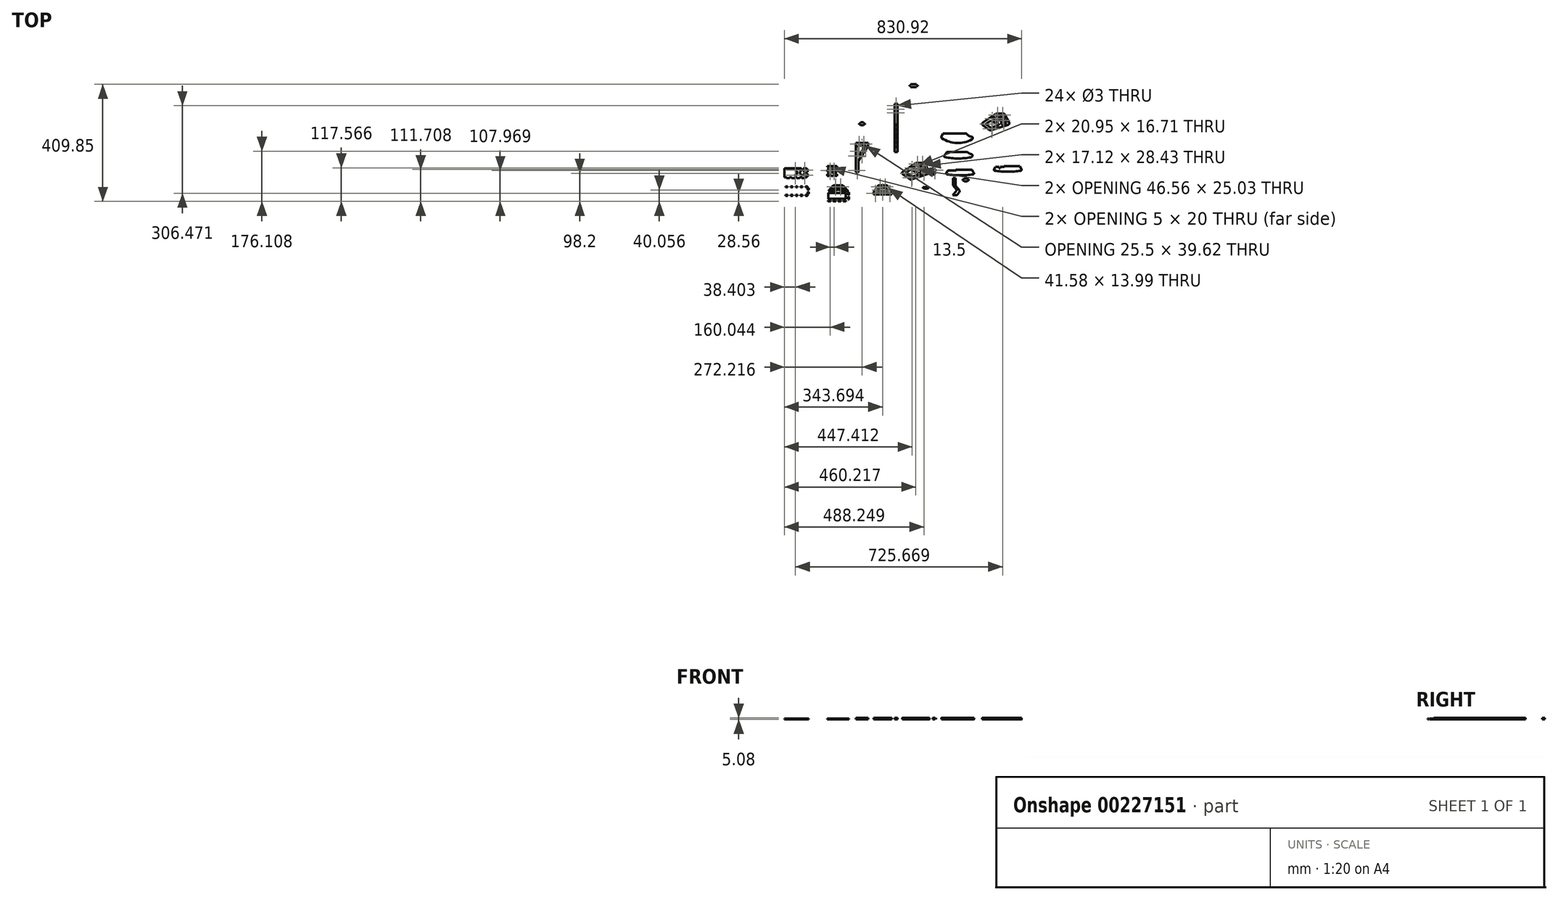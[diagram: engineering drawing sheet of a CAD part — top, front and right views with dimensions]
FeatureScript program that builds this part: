
annotation { "Feature Type Name" : "Feature", "Feature Type Description" : "" }
export const myFeature = defineFeature(function(context is Context, id is Id, definition is map)
    precondition{}
    {
        {
            var Q0;
            Q0=qCreatedBy(makeId("Top.planeOp"),FACE);
            var sketch = newSketch(context, id + "F0", { "sketchPlane" : qUnion([Q0])});
            skCircle(sketch, "E0", {"center": v(-57.8, 43.26) * mm, "radius": 1.5 * mm});
            skLineSegment(sketch, "E1.MirrorCS", {"start": v(-51.3, 50.26) * mm, "end": v(-51.3, 18.26) * mm});
            skLineSegment(sketch, "E2.MirrorCS", {"start": v(-51.3, 47.26) * mm, "end": v(-48.13, 47.26) * mm});
            skLineSegment(sketch, "E3.MirrorCS", {"start": v(-48.13, 47.26) * mm, "end": v(-48.13, 37.26) * mm});
            skLineSegment(sketch, "E4.MirrorCS", {"start": v(-48.13, 37.26) * mm, "end": v(-51.3, 37.26) * mm});
            skLineSegment(sketch, "E5.MirrorCS", {"start": v(-48.13, 31.26) * mm, "end": v(-51.3, 31.26) * mm});
            skLineSegment(sketch, "E6.MirrorCS", {"start": v(-48.13, 21.26) * mm, "end": v(-48.13, 31.26) * mm});
            skLineSegment(sketch, "E7.MirrorCS", {"start": v(-51.3, 21.26) * mm, "end": v(-48.13, 21.26) * mm});
            skCircle(sketch, "E8", {"center": v(-66.8, 34.26) * mm, "radius": 8 * mm});
            skLineSegment(sketch, "E9", {"start": v(-129.3, 50.26) * mm, "end": v(-129.3, 18.26) * mm});
            skLineSegment(sketch, "E10", {"start": v(-121.7, 18.26) * mm, "end": v(-121.7, 15.09) * mm});
            skLineSegment(sketch, "E11", {"start": v(-121.7, 15.09) * mm, "end": v(-111.7, 15.09) * mm});
            skLineSegment(sketch, "E12", {"start": v(-111.7, 15.09) * mm, "end": v(-111.7, 18.26) * mm});
            skLineSegment(sketch, "E13", {"start": v(-104.1, 18.26) * mm, "end": v(-104.1, 15.09) * mm});
            skLineSegment(sketch, "E14", {"start": v(-104.1, 15.09) * mm, "end": v(-94.1, 15.09) * mm});
            skLineSegment(sketch, "E15", {"start": v(-94.1, 15.09) * mm, "end": v(-94.1, 18.26) * mm});
            skLineSegment(sketch, "E16", {"start": v(-86.5, 18.26) * mm, "end": v(-86.5, 15.09) * mm});
            skLineSegment(sketch, "E17", {"start": v(-86.5, 15.09) * mm, "end": v(-76.5, 15.09) * mm});
            skLineSegment(sketch, "E18", {"start": v(-76.5, 15.09) * mm, "end": v(-76.5, 18.26) * mm});
            skLineSegment(sketch, "E19", {"start": v(-68.9, 18.26) * mm, "end": v(-68.9, 15.09) * mm});
            skLineSegment(sketch, "E20", {"start": v(-68.9, 15.09) * mm, "end": v(-58.9, 15.09) * mm});
            skLineSegment(sketch, "E21", {"start": v(-58.9, 15.09) * mm, "end": v(-58.9, 18.26) * mm});
            skCircle(sketch, "E22", {"center": v(-57.8, 43.26) * mm, "radius": 4 * mm, "construction": true});
            skCircle(sketch, "E23", {"center": v(-57.8, 25.36) * mm, "radius": 1.5 * mm});
            skCircle(sketch, "E24", {"center": v(-57.8, 25.36) * mm, "radius": 4 * mm, "construction": true});
            skLineSegment(sketch, "E25", {"start": v(-57.8, 47.26) * mm, "end": v(-57.8, 21.36) * mm, "construction": true});
            skCircle(sketch, "E26", {"center": v(-90.9, 43.26) * mm, "radius": 1.5 * mm});
            skCircle(sketch, "E27", {"center": v(-90.9, 43.26) * mm, "radius": 4 * mm, "construction": true});
            skLineSegment(sketch, "E28", {"start": v(-53.8, 43.26) * mm, "end": v(-94.9, 43.26) * mm, "construction": true});
            skCircle(sketch, "E29", {"center": v(-90.9, 25.36) * mm, "radius": 4 * mm, "construction": true});
            skCircle(sketch, "E30", {"center": v(-90.9, 25.36) * mm, "radius": 1.5 * mm});
            skLineSegment(sketch, "E31", {"start": v(-90.9, 47.26) * mm, "end": v(-90.9, 21.36) * mm, "construction": true});
            skLineSegment(sketch, "E32", {"start": v(-94.9, 25.36) * mm, "end": v(-53.8, 25.36) * mm, "construction": true});
            skCircle(sketch, "E33", {"center": v(-66.8, 34.26) * mm, "radius": 3 * mm});
            skLineSegment(sketch, "E34", {"start": v(-63.8, 34.26) * mm, "end": v(-63.8, 50.26) * mm});
            skLineSegment(sketch, "E35", {"start": v(-69.8, 34.26) * mm, "end": v(-69.8, 50.26) * mm});
            skPoint(sketch, "E36.middle.positionSnap0", {"position": v(-129.3, 34.26) * mm});
            skPoint(sketch, "E36.centerSnap0", {"position": v(-129.3, 34.26) * mm});
            skLineSegment(sketch, "E37", {"start": v(-129.3, 34.26) * mm, "end": v(-51.3, 34.26) * mm, "construction": true});
            skPoint(sketch, "E38.middle", {"position": v(-88.64, 39.7) * mm});
            skLineSegment(sketch, "E39.bottom", {"start": v(-84.41, 39.34) * mm, "end": v(-87.41, 39.34) * mm});
            skLineSegment(sketch, "E39.top", {"start": v(-84.41, 29.18) * mm, "end": v(-87.41, 29.18) * mm});
            skLineSegment(sketch, "E39.left", {"start": v(-84.41, 39.34) * mm, "end": v(-84.41, 29.18) * mm});
            skLineSegment(sketch, "E39.right", {"start": v(-87.41, 39.34) * mm, "end": v(-87.41, 29.18) * mm});
            skPoint(sketch, "E39.middle", {"position": v(-85.91, 34.26) * mm});
            skLineSegment(sketch, "E40.bottom", {"start": v(-47.84, -16.11) * mm, "end": v(-125.84, -16.11) * mm});
            skLineSegment(sketch, "E40.top", {"start": v(-47.84, -43.11) * mm, "end": v(-125.84, -43.11) * mm});
            skLineSegment(sketch, "E40.left", {"start": v(-47.84, -16.11) * mm, "end": v(-47.84, -43.11) * mm});
            skLineSegment(sketch, "E41.bottom", {"start": v(-47.84, -19.11) * mm, "end": v(-44.66, -19.11) * mm});
            skLineSegment(sketch, "E41.top", {"start": v(-47.84, -26.61) * mm, "end": v(-44.66, -26.61) * mm});
            skLineSegment(sketch, "E41.left", {"start": v(-47.84, -19.11) * mm, "end": v(-47.84, -26.61) * mm});
            skLineSegment(sketch, "E41.right", {"start": v(-44.66, -19.11) * mm, "end": v(-44.66, -26.61) * mm});
            skLineSegment(sketch, "E42", {"start": v(-125.84, -43.11) * mm, "end": v(-125.84, -46.29) * mm});
            skLineSegment(sketch, "E43", {"start": v(-125.84, -46.29) * mm, "end": v(-118.24, -46.29) * mm});
            skLineSegment(sketch, "E44", {"start": v(-118.24, -46.29) * mm, "end": v(-118.24, -43.11) * mm});
            skLineSegment(sketch, "E45", {"start": v(-108.24, -43.11) * mm, "end": v(-108.24, -46.27) * mm});
            skLineSegment(sketch, "E46", {"start": v(-108.24, -46.27) * mm, "end": v(-100.64, -46.27) * mm});
            skLineSegment(sketch, "E47", {"start": v(-100.64, -46.27) * mm, "end": v(-100.64, -43.1) * mm});
            skLineSegment(sketch, "E48", {"start": v(-90.64, -43.11) * mm, "end": v(-90.64, -46.27) * mm});
            skLineSegment(sketch, "E49", {"start": v(-90.64, -46.27) * mm, "end": v(-83.04, -46.27) * mm});
            skLineSegment(sketch, "E50", {"start": v(-83.04, -46.27) * mm, "end": v(-83.04, -43.11) * mm});
            skLineSegment(sketch, "E51", {"start": v(-73.04, -43.11) * mm, "end": v(-73.04, -46.29) * mm});
            skLineSegment(sketch, "E52", {"start": v(-73.04, -46.29) * mm, "end": v(-65.44, -46.29) * mm});
            skLineSegment(sketch, "E53", {"start": v(-65.44, -46.29) * mm, "end": v(-65.44, -43.11) * mm});
            skLineSegment(sketch, "E54", {"start": v(-55.44, -43.11) * mm, "end": v(-55.44, -46.29) * mm});
            skLineSegment(sketch, "E55", {"start": v(-55.44, -46.29) * mm, "end": v(-47.84, -46.29) * mm});
            skLineSegment(sketch, "E56", {"start": v(-47.84, -46.29) * mm, "end": v(-47.84, -43.11) * mm});
            skLineSegment(sketch, "E57", {"start": v(-125.84, -43.11) * mm, "end": v(-125.84, -16.11) * mm});
            skLineSegment(sketch, "E58.MirrorCS", {"start": v(-125.84, -12.94) * mm, "end": v(-118.24, -12.94) * mm});
            skLineSegment(sketch, "E59.MirrorCS", {"start": v(-125.84, -16.11) * mm, "end": v(-125.84, -12.94) * mm});
            skLineSegment(sketch, "E60.MirrorCS", {"start": v(-118.24, -12.94) * mm, "end": v(-118.24, -16.11) * mm});
            skLineSegment(sketch, "E61.MirrorCS", {"start": v(-108.24, -12.96) * mm, "end": v(-100.64, -12.96) * mm});
            skLineSegment(sketch, "E62.MirrorCS", {"start": v(-108.24, -16.11) * mm, "end": v(-108.24, -12.96) * mm});
            skLineSegment(sketch, "E63.MirrorCS", {"start": v(-100.64, -12.96) * mm, "end": v(-100.64, -16.13) * mm});
            skLineSegment(sketch, "E64.MirrorCS", {"start": v(-90.64, -12.96) * mm, "end": v(-83.04, -12.96) * mm});
            skLineSegment(sketch, "E65.MirrorCS", {"start": v(-90.64, -16.11) * mm, "end": v(-90.64, -12.96) * mm});
            skLineSegment(sketch, "E66.MirrorCS", {"start": v(-83.04, -12.96) * mm, "end": v(-83.04, -16.11) * mm});
            skLineSegment(sketch, "E67.MirrorCS", {"start": v(-73.04, -12.94) * mm, "end": v(-65.44, -12.94) * mm});
            skLineSegment(sketch, "E68.MirrorCS", {"start": v(-73.04, -16.11) * mm, "end": v(-73.04, -12.94) * mm});
            skLineSegment(sketch, "E69.MirrorCS", {"start": v(-65.44, -12.94) * mm, "end": v(-65.44, -16.11) * mm});
            skLineSegment(sketch, "E70.MirrorCS", {"start": v(-55.44, -16.11) * mm, "end": v(-55.44, -12.94) * mm});
            skLineSegment(sketch, "E71.MirrorCS", {"start": v(-55.44, -12.94) * mm, "end": v(-47.84, -12.94) * mm});
            skLineSegment(sketch, "E72.MirrorCS", {"start": v(-47.84, -12.94) * mm, "end": v(-47.84, -16.11) * mm});
            skLineSegment(sketch, "E73.MirrorCS", {"start": v(-47.84, -32.61) * mm, "end": v(-44.66, -32.61) * mm});
            skLineSegment(sketch, "E74.MirrorCS", {"start": v(-44.66, -40.11) * mm, "end": v(-44.66, -32.61) * mm});
            skLineSegment(sketch, "E75.MirrorCS", {"start": v(-47.84, -40.11) * mm, "end": v(-44.66, -40.11) * mm});
            skLineSegment(sketch, "E76.MirrorCS", {"start": v(93.67, -30.61) * mm, "end": v(93.67, -62.61) * mm});
            skLineSegment(sketch, "E77.MirrorCS", {"start": v(97.56, -25.43) * mm, "end": v(98.56, -25.43) * mm});
            skLineSegment(sketch, "E78.MirrorCS", {"start": v(96.85, -33.61) * mm, "end": v(96.85, -43.61) * mm});
            skLineSegment(sketch, "E79.MirrorCS", {"start": v(96.85, -59.61) * mm, "end": v(96.85, -49.61) * mm});
            skLineSegment(sketch, "E80", {"start": v(15.67, -30.61) * mm, "end": v(15.67, -62.61) * mm});
            skLineSegment(sketch, "E81", {"start": v(23.27, -62.61) * mm, "end": v(23.27, -65.79) * mm});
            skLineSegment(sketch, "E82", {"start": v(23.27, -65.79) * mm, "end": v(33.27, -65.79) * mm});
            skLineSegment(sketch, "E83", {"start": v(33.27, -65.79) * mm, "end": v(33.27, -62.61) * mm});
            skLineSegment(sketch, "E84", {"start": v(40.87, -62.61) * mm, "end": v(40.87, -65.79) * mm});
            skLineSegment(sketch, "E85", {"start": v(40.87, -65.79) * mm, "end": v(50.87, -65.79) * mm});
            skLineSegment(sketch, "E86", {"start": v(50.87, -65.79) * mm, "end": v(50.87, -62.61) * mm});
            skLineSegment(sketch, "E87", {"start": v(58.47, -62.61) * mm, "end": v(58.47, -65.79) * mm});
            skLineSegment(sketch, "E88", {"start": v(58.47, -65.79) * mm, "end": v(68.47, -65.79) * mm});
            skLineSegment(sketch, "E89", {"start": v(68.47, -65.79) * mm, "end": v(68.47, -62.61) * mm});
            skLineSegment(sketch, "E90", {"start": v(76.07, -62.61) * mm, "end": v(76.07, -65.79) * mm});
            skLineSegment(sketch, "E91", {"start": v(76.07, -65.79) * mm, "end": v(86.07, -65.79) * mm});
            skLineSegment(sketch, "E92", {"start": v(86.07, -65.79) * mm, "end": v(86.07, -62.61) * mm});
            skLineSegment(sketch, "E93", {"start": v(15.67, -30.61) * mm, "end": v(93.67, -30.61) * mm});
            skLineSegment(sketch, "E94", {"start": v(15.67, -62.61) * mm, "end": v(93.67, -62.61) * mm});
            skLineSegment(sketch, "E95", {"start": v(96.85, -33.61) * mm, "end": v(93.67, -33.61) * mm});
            skLineSegment(sketch, "E96", {"start": v(96.85, -43.61) * mm, "end": v(93.67, -43.61) * mm});
            skLineSegment(sketch, "E97", {"start": v(96.85, -49.61) * mm, "end": v(93.67, -49.61) * mm});
            skLineSegment(sketch, "E98", {"start": v(96.85, -59.61) * mm, "end": v(93.67, -59.61) * mm});
            skLineSegment(sketch, "E99.left", {"start": v(15.67, -62.61) * mm, "end": v(15.67, -30.61) * mm});
            skLineSegment(sketch, "E100.bottom", {"start": v(75.3, -9.86) * mm, "end": v(42.75, -9.86) * mm});
            skLineSegment(sketch, "E100.left", {"start": v(75.3, -9.86) * mm, "end": v(75.3, -18.86) * mm});
            skLineSegment(sketch, "E100.right", {"start": v(42.75, -9.86) * mm, "end": v(42.75, -18.86) * mm});
            skPoint(sketch, "E100.middle", {"position": v(59.03, -14.36) * mm});
            skCircle(sketch, "E101", {"center": v(67.78, -14.36) * mm, "radius": 1.5 * mm});
            skCircle(sketch, "E102.MirrorC", {"center": v(50.28, -14.36) * mm, "radius": 1.5 * mm});
            skLineSegment(sketch, "E103", {"start": v(42.75, -18.86) * mm, "end": v(42.75, -30.61) * mm});
            skLineSegment(sketch, "E104", {"start": v(75.3, -18.86) * mm, "end": v(75.3, -30.61) * mm});
            skPoint(sketch, "E105.middle", {"position": v(54.67, -46.61) * mm});
            skPoint(sketch, "E105.middle.positionSnap0", {"position": v(54.67, -30.61) * mm});
            skPoint(sketch, "E105.middle.positionSnap1", {"position": v(15.67, -46.61) * mm});
            skPoint(sketch, "E105.centerSnap0", {"position": v(54.67, -30.61) * mm});
            skPoint(sketch, "E105.centerSnap1", {"position": v(15.67, -46.61) * mm});
            skLineSegment(sketch, "E106", {"start": v(75.3, -9.86) * mm, "end": v(93.67, -30.61) * mm});
            skLineSegment(sketch, "E107.bottom", {"start": v(50.98, 58.18) * mm, "end": v(23.98, 58.18) * mm});
            skLineSegment(sketch, "E107.top", {"start": v(50.98, 26.18) * mm, "end": v(23.98, 26.18) * mm});
            skLineSegment(sketch, "E107.left", {"start": v(50.98, 58.18) * mm, "end": v(50.98, 26.18) * mm});
            skLineSegment(sketch, "E107.right", {"start": v(23.98, 58.18) * mm, "end": v(23.98, 26.18) * mm});
            skPoint(sketch, "E107.middle", {"position": v(37.48, 42.18) * mm});
            skLineSegment(sketch, "E108", {"start": v(37.48, 58.18) * mm, "end": v(37.48, 26.18) * mm, "construction": true});
            skLineSegment(sketch, "E109", {"start": v(34.48, 26.18) * mm, "end": v(34.48, 23) * mm});
            skLineSegment(sketch, "E110", {"start": v(34.48, 23) * mm, "end": v(40.48, 23) * mm});
            skLineSegment(sketch, "E111", {"start": v(40.48, 23) * mm, "end": v(40.48, 26.18) * mm});
            skLineSegment(sketch, "E112", {"start": v(47.98, 23) * mm, "end": v(47.98, 26.18) * mm});
            skLineSegment(sketch, "E113", {"start": v(50.98, 45.18) * mm, "end": v(54.3, 45.18) * mm});
            skLineSegment(sketch, "E114", {"start": v(54.3, 45.18) * mm, "end": v(54.3, 39.18) * mm});
            skLineSegment(sketch, "E115", {"start": v(54.3, 39.18) * mm, "end": v(50.98, 39.18) * mm});
            skLineSegment(sketch, "E116", {"start": v(50.98, 58.18) * mm, "end": v(54.3, 58.18) * mm});
            skLineSegment(sketch, "E117", {"start": v(54.3, 58.18) * mm, "end": v(54.3, 55.18) * mm});
            skLineSegment(sketch, "E118", {"start": v(54.3, 55.18) * mm, "end": v(50.98, 55.18) * mm});
            skLineSegment(sketch, "E119", {"start": v(23.98, 42.18) * mm, "end": v(50.98, 42.18) * mm, "construction": true});
            skLineSegment(sketch, "E120.MirrorCS", {"start": v(54.3, 29.18) * mm, "end": v(50.98, 29.18) * mm});
            skLineSegment(sketch, "E121.MirrorCS", {"start": v(54.3, 26.18) * mm, "end": v(54.3, 29.18) * mm});
            skLineSegment(sketch, "E122.MirrorCS", {"start": v(50.98, 26.18) * mm, "end": v(54.3, 26.18) * mm});
            skLineSegment(sketch, "E123.MirrorCS", {"start": v(23.98, 58.18) * mm, "end": v(20.67, 58.18) * mm});
            skLineSegment(sketch, "E124.MirrorCS", {"start": v(20.67, 55.18) * mm, "end": v(23.98, 55.18) * mm});
            skLineSegment(sketch, "E125.MirrorCS", {"start": v(20.67, 58.18) * mm, "end": v(20.67, 55.18) * mm});
            skLineSegment(sketch, "E126.MirrorCS", {"start": v(23.98, 45.18) * mm, "end": v(20.67, 45.18) * mm});
            skLineSegment(sketch, "E127.MirrorCS", {"start": v(20.67, 45.18) * mm, "end": v(20.67, 39.18) * mm});
            skLineSegment(sketch, "E128.MirrorCS", {"start": v(20.67, 39.18) * mm, "end": v(23.98, 39.18) * mm});
            skLineSegment(sketch, "E129.MirrorCS", {"start": v(20.67, 29.18) * mm, "end": v(23.98, 29.18) * mm});
            skLineSegment(sketch, "E130.MirrorCS", {"start": v(23.98, 26.18) * mm, "end": v(20.67, 26.18) * mm});
            skLineSegment(sketch, "E131.MirrorCS", {"start": v(20.67, 26.18) * mm, "end": v(20.67, 29.18) * mm});
            skLineSegment(sketch, "E132", {"start": v(47.98, 23) * mm, "end": v(54.3, 23) * mm});
            skLineSegment(sketch, "E133", {"start": v(54.3, 23) * mm, "end": v(54.3, 26.18) * mm});
            skLineSegment(sketch, "E134.MirrorCS", {"start": v(26.98, 23) * mm, "end": v(26.98, 26.18) * mm});
            skLineSegment(sketch, "E135.MirrorCS", {"start": v(26.98, 23) * mm, "end": v(20.67, 23) * mm});
            skLineSegment(sketch, "E136.MirrorCS", {"start": v(20.67, 23) * mm, "end": v(20.67, 26.18) * mm});
            skLineSegment(sketch, "E137", {"start": v(-86.84, -16.11) * mm, "end": v(-86.84, -43.11) * mm, "construction": true});
            skLineSegment(sketch, "E138", {"start": v(-125.84, -29.61) * mm, "end": v(-47.84, -29.61) * mm, "construction": true});
            skLineSegment(sketch, "E139", {"start": v(-129.3, 50.26) * mm, "end": v(-51.3, 50.26) * mm});
            skLineSegment(sketch, "E140", {"start": v(-129.3, 18.26) * mm, "end": v(-51.3, 18.26) * mm});
            skCircle(sketch, "E141", {"center": v(125.66, 93.63) * mm, "radius": 1.5 * mm});
            skCircle(sketch, "E142", {"center": v(125.66, 42.93) * mm, "radius": 1.5 * mm});
            skLineSegment(sketch, "E143", {"start": v(125.66, 93.63) * mm, "end": v(125.66, 42.93) * mm});
            skPoint(sketch, "E144.middle", {"position": v(125.66, 68.28) * mm});
            skLineSegment(sketch, "E145.top", {"start": v(121.16, 139.13) * mm, "end": v(155.66, 139.13) * mm});
            skLineSegment(sketch, "E145.left", {"start": v(121.16, 130.13) * mm, "end": v(121.16, 139.13) * mm});
            skLineSegment(sketch, "E145.right", {"start": v(155.66, 130.13) * mm, "end": v(155.66, 139.13) * mm});
            skCircle(sketch, "E146", {"center": v(131.66, 134.63) * mm, "radius": 1.5 * mm});
            skPoint(sketch, "E146.centerSnap0", {"position": v(121.16, 134.63) * mm});
            skLineSegment(sketch, "E147", {"start": v(131.66, 134.63) * mm, "end": v(149.16, 134.63) * mm});
            skCircle(sketch, "E148", {"center": v(149.16, 134.63) * mm, "radius": 1.5 * mm});
            skLineSegment(sketch, "E149", {"start": v(121.16, 130.13) * mm, "end": v(155.66, 130.13) * mm});
            skLineSegment(sketch, "E150", {"start": v(121.16, 130.13) * mm, "end": v(121.16, 36.43) * mm});
            skLineSegment(sketch, "E151", {"start": v(121.16, 36.43) * mm, "end": v(130.16, 36.43) * mm});
            skLineSegment(sketch, "E152", {"start": v(130.16, 36.43) * mm, "end": v(130.16, 130.13) * mm});
            skLineSegment(sketch, "E153", {"start": v(164.66, 130.13) * mm, "end": v(130.16, 76.52) * mm});
            skLineSegment(sketch, "E154", {"start": v(155.66, 130.13) * mm, "end": v(130.16, 90.5) * mm});
            skLineSegment(sketch, "E155", {"start": v(164.66, 130.13) * mm, "end": v(164.66, 139.13) * mm});
            skLineSegment(sketch, "E156", {"start": v(164.66, 139.13) * mm, "end": v(155.66, 139.13) * mm});
            skLineSegment(sketch, "E157.bottom", {"start": v(182.48, -32.73) * mm, "end": v(246.28, -32.73) * mm});
            skLineSegment(sketch, "E157.top", {"start": v(182.48, -41.73) * mm, "end": v(246.28, -41.73) * mm});
            skLineSegment(sketch, "E157.left", {"start": v(182.48, -32.73) * mm, "end": v(182.48, -41.73) * mm});
            skLineSegment(sketch, "E157.right", {"start": v(246.28, -32.73) * mm, "end": v(246.28, -41.73) * mm});
            skCircle(sketch, "E158", {"center": v(188.98, -37.23) * mm, "radius": 1.5 * mm});
            skPoint(sketch, "E158.centerSnap0", {"position": v(182.48, -37.23) * mm});
            skCircle(sketch, "E159", {"center": v(239.78, -37.23) * mm, "radius": 1.5 * mm});
            skLineSegment(sketch, "E160.bottom", {"start": v(199.13, -9.74) * mm, "end": v(229.63, -9.74) * mm});
            skLineSegment(sketch, "E160.top", {"start": v(199.13, -18.74) * mm, "end": v(229.63, -18.74) * mm});
            skLineSegment(sketch, "E160.left", {"start": v(199.13, -9.74) * mm, "end": v(199.13, -18.74) * mm});
            skLineSegment(sketch, "E160.right", {"start": v(229.63, -9.74) * mm, "end": v(229.63, -18.74) * mm});
            skLineSegment(sketch, "E161", {"start": v(199.13, -9.74) * mm, "end": v(182.48, -32.73) * mm});
            skLineSegment(sketch, "E162", {"start": v(199.13, -18.74) * mm, "end": v(189, -32.73) * mm, "construction": true});
            skLineSegment(sketch, "E163", {"start": v(229.63, -9.74) * mm, "end": v(246.28, -32.73) * mm});
            skLineSegment(sketch, "E164", {"start": v(229.63, -18.74) * mm, "end": v(239.77, -32.73) * mm, "construction": true});
            skCircle(sketch, "E165", {"center": v(205.63, -14.24) * mm, "radius": 1.5 * mm});
            skPoint(sketch, "E165.centerSnap0", {"position": v(199.13, -14.24) * mm});
            skCircle(sketch, "E166", {"center": v(223.13, -14.24) * mm, "radius": 1.5 * mm});
            skPoint(sketch, "E166.centerSnap0", {"position": v(229.63, -14.24) * mm});
            skLineSegment(sketch, "E167", {"start": v(214.38, -18.74) * mm, "end": v(214.38, -32.73) * mm, "construction": true});
            skLineSegment(sketch, "E168", {"start": v(193.6, -32.73) * mm, "end": v(203.73, -18.74) * mm});
            skLineSegment(sketch, "E169.MirrorCS", {"start": v(235.17, -32.73) * mm, "end": v(225.04, -18.74) * mm});
            skLineSegment(sketch, "E170.bottom", {"start": v(330.61, 69.13) * mm, "end": v(361.11, 69.13) * mm});
            skLineSegment(sketch, "E170.top", {"start": v(330.61, 60.13) * mm, "end": v(361.11, 60.13) * mm});
            skLineSegment(sketch, "E170.left", {"start": v(330.61, 69.13) * mm, "end": v(330.61, 60.13) * mm});
            skLineSegment(sketch, "E170.right", {"start": v(361.11, 69.13) * mm, "end": v(361.11, 60.13) * mm});
            skCircle(sketch, "E171", {"center": v(337.11, 64.63) * mm, "radius": 1.5 * mm});
            skPoint(sketch, "E171.centerSnap0", {"position": v(330.61, 64.63) * mm});
            skCircle(sketch, "E172", {"center": v(354.61, 64.63) * mm, "radius": 1.5 * mm});
            skPoint(sketch, "E172.centerSnap0", {"position": v(361.11, 64.63) * mm});
            skLineSegment(sketch, "E173", {"start": v(354.61, 64.63) * mm, "end": v(364.99, 32.38) * mm, "construction": true});
            skCircle(sketch, "E174", {"center": v(364.99, 32.38) * mm, "radius": 2.25 * mm});
            skLineSegment(sketch, "E175", {"start": v(364.99, 32.38) * mm, "end": v(316.44, 16.76) * mm, "construction": true});
            skCircle(sketch, "E176", {"center": v(316.44, 16.76) * mm, "radius": 1.5 * mm});
            skLineSegment(sketch, "E177", {"start": v(309.08, 18.42) * mm, "end": v(311.72, 10.2) * mm});
            skLineSegment(sketch, "E178", {"start": v(311.72, 10.2) * mm, "end": v(373.36, 30.03) * mm});
            skLineSegment(sketch, "E179", {"start": v(373.36, 30.03) * mm, "end": v(370.72, 38.25) * mm});
            skLineSegment(sketch, "E180", {"start": v(370.72, 38.25) * mm, "end": v(309.08, 18.42) * mm});
            skLineSegment(sketch, "E181", {"start": v(361.11, 69.13) * mm, "end": v(380.2, 32.23) * mm});
            skLineSegment(sketch, "E182", {"start": v(380.2, 32.23) * mm, "end": v(373.36, 30.03) * mm});
            skLineSegment(sketch, "E183", {"start": v(367.5, 37.21) * mm, "end": v(355.64, 60.13) * mm});
            skLineSegment(sketch, "E184", {"start": v(309.08, 18.42) * mm, "end": v(304.62, 7.92) * mm});
            skLineSegment(sketch, "E185", {"start": v(304.62, 7.92) * mm, "end": v(311.72, 10.2) * mm});
            skCircle(sketch, "E186", {"center": v(397.86, 43.41) * mm, "radius": 1.5 * mm});
            skCircle(sketch, "E187", {"center": v(397.86, 43.41) * mm, "radius": 3 * mm});
            skCircle(sketch, "E188", {"center": v(394.3, 31.54) * mm, "radius": 2.25 * mm});
            skCircle(sketch, "E189", {"center": v(394.3, 31.54) * mm, "radius": 3.75 * mm});
            skLineSegment(sketch, "E190.bottom", {"start": v(257.06, 256.54) * mm, "end": v(267.22, 256.54) * mm});
            skLineSegment(sketch, "E190.top", {"start": v(257.06, 106.54) * mm, "end": v(267.22, 106.54) * mm});
            skLineSegment(sketch, "E190.left", {"start": v(257.06, 256.54) * mm, "end": v(257.06, 106.54) * mm});
            skLineSegment(sketch, "E190.right", {"start": v(267.22, 256.54) * mm, "end": v(267.22, 106.54) * mm});
            skCircle(sketch, "E191", {"center": v(262.14, 256.54) * mm, "radius": 1.5 * mm});
            skCircle(sketch, "E192", {"center": v(262.14, 243.84) * mm, "radius": 1.5 * mm});
            skLineSegment(sketch, "E193", {"start": v(257.06, 256.54) * mm, "end": v(257.06, 276.54) * mm});
            skLineSegment(sketch, "E194", {"start": v(257.06, 276.54) * mm, "end": v(267.22, 276.54) * mm});
            skLineSegment(sketch, "E195", {"start": v(267.22, 276.54) * mm, "end": v(267.22, 256.54) * mm});
            skCircle(sketch, "E196.MirrorC", {"center": v(262.14, 269.24) * mm, "radius": 1.5 * mm});
            skPoint(sketch, "E197.centerSnap0", {"position": v(262.14, 106.54) * mm});
            skLineSegment(sketch, "E198.bottom", {"start": v(264.14, 203.84) * mm, "end": v(260.14, 203.84) * mm});
            skLineSegment(sketch, "E198.top", {"start": v(264.14, 198.76) * mm, "end": v(260.14, 198.76) * mm});
            skLineSegment(sketch, "E198.left", {"start": v(264.14, 203.84) * mm, "end": v(264.14, 198.76) * mm});
            skLineSegment(sketch, "E198.right", {"start": v(260.14, 203.84) * mm, "end": v(260.14, 198.76) * mm});
            skPoint(sketch, "E198.middle", {"position": v(262.14, 201.3) * mm});
            skLineSegment(sketch, "E199.bottom", {"start": v(264.14, 188.76) * mm, "end": v(260.14, 188.76) * mm});
            skLineSegment(sketch, "E199.top", {"start": v(264.14, 183.68) * mm, "end": v(260.14, 183.68) * mm});
            skLineSegment(sketch, "E199.left", {"start": v(264.14, 188.76) * mm, "end": v(264.14, 183.68) * mm});
            skLineSegment(sketch, "E199.right", {"start": v(260.14, 188.76) * mm, "end": v(260.14, 183.68) * mm});
            skPoint(sketch, "E199.middle", {"position": v(262.14, 186.22) * mm});
            skPoint(sketch, "E199.middle.positionSnap0", {"position": v(262.14, 198.76) * mm});
            skPoint(sketch, "E199.centerSnap0", {"position": v(262.14, 198.76) * mm});
            skLineSegment(sketch, "E200.bottom", {"start": v(264.14, 173.68) * mm, "end": v(260.14, 173.68) * mm});
            skLineSegment(sketch, "E200.top", {"start": v(264.14, 168.6) * mm, "end": v(260.14, 168.6) * mm});
            skLineSegment(sketch, "E200.left", {"start": v(264.14, 173.68) * mm, "end": v(264.14, 168.6) * mm});
            skLineSegment(sketch, "E200.right", {"start": v(260.14, 173.68) * mm, "end": v(260.14, 168.6) * mm});
            skPoint(sketch, "E200.middle", {"position": v(262.14, 171.14) * mm});
            skPoint(sketch, "E200.middle.positionSnap0", {"position": v(262.14, 183.68) * mm});
            skPoint(sketch, "E200.centerSnap0", {"position": v(262.14, 183.68) * mm});
            skLineSegment(sketch, "E201.bottom", {"start": v(264.14, 158.6) * mm, "end": v(260.14, 158.6) * mm});
            skLineSegment(sketch, "E201.top", {"start": v(264.14, 153.52) * mm, "end": v(260.14, 153.52) * mm});
            skLineSegment(sketch, "E201.left", {"start": v(264.14, 158.6) * mm, "end": v(264.14, 153.52) * mm});
            skLineSegment(sketch, "E201.right", {"start": v(260.14, 158.6) * mm, "end": v(260.14, 153.52) * mm});
            skPoint(sketch, "E201.middle", {"position": v(262.14, 156.06) * mm});
            skPoint(sketch, "E201.middle.positionSnap0", {"position": v(262.14, 168.6) * mm});
            skPoint(sketch, "E201.centerSnap0", {"position": v(262.14, 168.6) * mm});
            skPoint(sketch, "E202.middle.positionSnap0", {"position": v(262.14, 153.52) * mm});
            skPoint(sketch, "E202.centerSnap0", {"position": v(262.14, 153.52) * mm});
            skLineSegment(sketch, "E203.bottom", {"start": v(137.72, 210.77) * mm, "end": v(147.24, 210.77) * mm});
            skLineSegment(sketch, "E203.top", {"start": v(137.72, 200.6) * mm, "end": v(147.24, 200.6) * mm});
            skLineSegment(sketch, "E203.left", {"start": v(137.72, 210.77) * mm, "end": v(137.72, 200.6) * mm});
            skLineSegment(sketch, "E203.right", {"start": v(147.24, 210.77) * mm, "end": v(147.24, 200.6) * mm});
            skLineSegment(sketch, "E204.bottom", {"start": v(147.24, 207.69) * mm, "end": v(152.32, 207.69) * mm});
            skLineSegment(sketch, "E204.top", {"start": v(147.24, 203.69) * mm, "end": v(152.32, 203.69) * mm});
            skLineSegment(sketch, "E204.left", {"start": v(147.24, 207.69) * mm, "end": v(147.24, 203.69) * mm});
            skLineSegment(sketch, "E204.right", {"start": v(152.32, 207.69) * mm, "end": v(152.32, 203.69) * mm});
            skLineSegment(sketch, "E205", {"start": v(142.48, 210.77) * mm, "end": v(142.48, 200.6) * mm, "construction": true});
            skLineSegment(sketch, "E206.MirrorCS", {"start": v(137.72, 207.69) * mm, "end": v(132.64, 207.69) * mm});
            skLineSegment(sketch, "E207.MirrorCS", {"start": v(132.64, 207.69) * mm, "end": v(132.64, 203.69) * mm});
            skLineSegment(sketch, "E208.MirrorCS", {"start": v(137.72, 203.69) * mm, "end": v(132.64, 203.69) * mm});
            skLineSegment(sketch, "E209", {"start": v(426.01, 171.7) * mm, "end": v(508.81, 171.7) * mm});
            skLineSegment(sketch, "E210", {"start": v(426.01, 171.7) * mm, "end": v(419.29, 157.26) * mm});
            skArc(sketch, "E211", {"start": v(508.81, 171.7) * mm, "mid": v(517.5, 163.5) * mm, "end": v(529.1, 160.7) * mm});
            skArc(sketch, "E212", {"start": v(529.09, 151.73) * mm, "mid": v(529.79, 156.21) * mm, "end": v(529.1, 160.7) * mm});
            skArc(sketch, "E213", {"start": v(419.29, 157.26) * mm, "mid": v(473.39, 138.7) * mm, "end": v(529.09, 151.73) * mm});
            skArc(sketch, "E214", {"start": v(427.52, 90.3) * mm, "mid": v(475.83, 84.48) * mm, "end": v(524.31, 88.6) * mm});
            skArc(sketch, "E215", {"start": v(524.31, 88.6) * mm, "mid": v(528.75, 92.71) * mm, "end": v(528.27, 98.75) * mm});
            skArc(sketch, "E216", {"start": v(510.32, 107.55) * mm, "mid": v(518.66, 101.85) * mm, "end": v(528.27, 98.75) * mm});
            skLineSegment(sketch, "E217", {"start": v(427.52, 90.3) * mm, "end": v(439.57, 107.55) * mm});
            skLineSegment(sketch, "E218", {"start": v(439.57, 107.55) * mm, "end": v(510.32, 107.55) * mm});
            skLineSegment(sketch, "E219", {"start": v(472.05, 45.33) * mm, "end": v(527.34, 45.33) * mm});
            skLineSegment(sketch, "E220", {"start": v(527.34, 45.33) * mm, "end": v(536.47, 29.52) * mm});
            skLineSegment(sketch, "E221", {"start": v(472.05, 45.33) * mm, "end": v(471.13, 41.92) * mm});
            skLineSegment(sketch, "E222", {"start": v(471.13, 41.92) * mm, "end": v(442.34, 41.92) * mm});
            skLineSegment(sketch, "E223", {"start": v(442.34, 41.92) * mm, "end": v(435.18, 29.52) * mm});
            skArc(sketch, "E224", {"start": v(435.18, 29.52) * mm, "mid": v(485.83, 25.33) * mm, "end": v(536.47, 29.52) * mm});
            skLineSegment(sketch, "E225", {"start": v(460.14, -44.05) * mm, "end": v(475.14, -44.05) * mm});
            skLineSegment(sketch, "E226", {"start": v(475.14, -44.05) * mm, "end": v(485.93, -31.18) * mm});
            skLineSegment(sketch, "E227", {"start": v(485.93, -31.18) * mm, "end": v(469.2, -9.36) * mm});
            skLineSegment(sketch, "E228", {"start": v(460.14, -44.05) * mm, "end": v(474.82, -26.55) * mm});
            skLineSegment(sketch, "E229", {"start": v(474.82, -26.55) * mm, "end": v(461.63, -9.36) * mm});
            skLineSegment(sketch, "E230", {"start": v(461.63, -9.36) * mm, "end": v(469.2, -9.36) * mm});
            skLineSegment(sketch, "E231", {"start": v(640.47, 58.15) * mm, "end": v(694.56, 58.15) * mm});
            skLineSegment(sketch, "E232", {"start": v(694.56, 58.15) * mm, "end": v(703.69, 42.34) * mm});
            skLineSegment(sketch, "E233", {"start": v(640.47, 58.15) * mm, "end": v(639.56, 54.74) * mm});
            skLineSegment(sketch, "E234", {"start": v(639.56, 54.74) * mm, "end": v(609.56, 54.74) * mm});
            skLineSegment(sketch, "E235", {"start": v(609.56, 54.74) * mm, "end": v(602.4, 42.34) * mm});
            skArc(sketch, "E236", {"start": v(602.4, 42.34) * mm, "mid": v(653.04, 38.15) * mm, "end": v(703.69, 42.34) * mm});
            skLineSegment(sketch, "E237.bottom", {"start": v(623.06, 54.74) * mm, "end": v(626.06, 54.74) * mm});
            skLineSegment(sketch, "E237.top", {"start": v(623.06, 49.74) * mm, "end": v(626.06, 49.74) * mm});
            skLineSegment(sketch, "E237.left", {"start": v(623.06, 54.74) * mm, "end": v(623.06, 49.74) * mm});
            skLineSegment(sketch, "E237.right", {"start": v(626.06, 54.74) * mm, "end": v(626.06, 49.74) * mm});
            skLineSegment(sketch, "E238.bottom", {"start": v(466.14, -44.05) * mm, "end": v(469.14, -44.05) * mm});
            skLineSegment(sketch, "E238.top", {"start": v(466.14, -49.05) * mm, "end": v(469.14, -49.05) * mm});
            skLineSegment(sketch, "E238.left", {"start": v(466.14, -44.05) * mm, "end": v(466.14, -49.05) * mm});
            skLineSegment(sketch, "E238.right", {"start": v(469.14, -44.05) * mm, "end": v(469.14, -49.05) * mm});
            skLineSegment(sketch, "E239", {"start": v(461.63, -9.36) * mm, "end": v(460.65, -9.36) * mm});
            skLineSegment(sketch, "E240", {"start": v(460.65, -9.36) * mm, "end": v(460.65, 15.64) * mm});
            skLineSegment(sketch, "E241", {"start": v(465.41, -9.36) * mm, "end": v(465.41, 15.64) * mm, "construction": true});
            skLineSegment(sketch, "E242", {"start": v(465.41, 15.64) * mm, "end": v(460.65, 15.64) * mm});
            skLineSegment(sketch, "E243.MirrorCS", {"start": v(469.2, -9.36) * mm, "end": v(470.17, -9.36) * mm});
            skLineSegment(sketch, "E244.MirrorCS", {"start": v(470.17, -9.36) * mm, "end": v(470.17, 15.64) * mm});
            skLineSegment(sketch, "E245.MirrorCS", {"start": v(465.41, 15.64) * mm, "end": v(470.17, 15.64) * mm});
            skLineSegment(sketch, "E246.bottom", {"start": v(361.27, -15.64) * mm, "end": v(370.8, -15.64) * mm});
            skLineSegment(sketch, "E246.top", {"start": v(361.27, -20.64) * mm, "end": v(370.8, -20.64) * mm});
            skLineSegment(sketch, "E246.left", {"start": v(361.27, -15.64) * mm, "end": v(361.27, -20.64) * mm});
            skLineSegment(sketch, "E246.right", {"start": v(370.8, -15.64) * mm, "end": v(370.8, -20.64) * mm});
            skLineSegment(sketch, "E247.bottom", {"start": v(370.8, -16.64) * mm, "end": v(375.88, -16.64) * mm});
            skLineSegment(sketch, "E247.top", {"start": v(370.8, -19.64) * mm, "end": v(375.88, -19.64) * mm});
            skLineSegment(sketch, "E247.left", {"start": v(370.8, -16.64) * mm, "end": v(370.8, -19.64) * mm});
            skLineSegment(sketch, "E247.right", {"start": v(375.88, -16.64) * mm, "end": v(375.88, -19.64) * mm});
            skLineSegment(sketch, "E248", {"start": v(366.03, -15.64) * mm, "end": v(366.03, -20.64) * mm, "construction": true});
            skLineSegment(sketch, "E249.MirrorCS", {"start": v(361.27, -16.64) * mm, "end": v(356.2, -16.64) * mm});
            skLineSegment(sketch, "E250.MirrorCS", {"start": v(356.2, -16.64) * mm, "end": v(356.2, -19.64) * mm});
            skLineSegment(sketch, "E251.MirrorCS", {"start": v(361.27, -19.64) * mm, "end": v(356.2, -19.64) * mm});
            skLineSegment(sketch, "E252.bottom", {"start": v(264.14, 138.44) * mm, "end": v(260.14, 138.44) * mm});
            skLineSegment(sketch, "E252.top", {"start": v(264.14, 143.52) * mm, "end": v(260.14, 143.52) * mm});
            skLineSegment(sketch, "E252.left", {"start": v(264.14, 138.44) * mm, "end": v(264.14, 143.52) * mm});
            skLineSegment(sketch, "E252.right", {"start": v(260.14, 138.44) * mm, "end": v(260.14, 143.52) * mm});
            skPoint(sketch, "E252.middle", {"position": v(262.14, 140.98) * mm});
            skLineSegment(sketch, "E253.bottom", {"start": v(510.5, 14.4) * mm, "end": v(500.97, 14.4) * mm});
            skLineSegment(sketch, "E253.top", {"start": v(510.5, 4.25) * mm, "end": v(500.97, 4.25) * mm});
            skLineSegment(sketch, "E253.left", {"start": v(510.5, 14.4) * mm, "end": v(510.5, 4.25) * mm});
            skLineSegment(sketch, "E253.right", {"start": v(500.97, 14.4) * mm, "end": v(500.97, 4.25) * mm});
            skPoint(sketch, "E253.middle", {"position": v(505.73, 9.33) * mm});
            skLineSegment(sketch, "E254.bottom", {"start": v(510.5, 11.33) * mm, "end": v(515.57, 11.33) * mm});
            skLineSegment(sketch, "E254.top", {"start": v(510.5, 7.33) * mm, "end": v(515.57, 7.33) * mm});
            skLineSegment(sketch, "E254.left", {"start": v(510.5, 11.33) * mm, "end": v(510.5, 7.33) * mm});
            skLineSegment(sketch, "E254.right", {"start": v(515.57, 11.33) * mm, "end": v(515.57, 7.33) * mm});
            skLineSegment(sketch, "E255", {"start": v(505.73, 4.25) * mm, "end": v(505.73, 14.4) * mm, "construction": true});
            skLineSegment(sketch, "E256.MirrorCS", {"start": v(500.97, 11.33) * mm, "end": v(495.89, 11.33) * mm});
            skLineSegment(sketch, "E257.MirrorCS", {"start": v(495.89, 11.33) * mm, "end": v(495.89, 7.33) * mm});
            skLineSegment(sketch, "E258.MirrorCS", {"start": v(500.97, 7.33) * mm, "end": v(495.89, 7.33) * mm});
            skLineSegment(sketch, "E259", {"start": v(345.88, 30.26) * mm, "end": v(345.88, 60.13) * mm});
            skLineSegment(sketch, "E260.bottom", {"start": v(347.38, 37.46) * mm, "end": v(344.38, 37.46) * mm});
            skLineSegment(sketch, "E260.top", {"start": v(347.38, 27.3) * mm, "end": v(344.38, 27.3) * mm});
            skLineSegment(sketch, "E260.left", {"start": v(347.38, 37.46) * mm, "end": v(347.38, 27.3) * mm});
            skLineSegment(sketch, "E260.right", {"start": v(344.38, 37.46) * mm, "end": v(344.38, 27.3) * mm});
            skPoint(sketch, "E260.middle", {"position": v(345.88, 32.38) * mm});
            skLineSegment(sketch, "E261", {"start": v(350.38, 31.7) * mm, "end": v(350.38, 60.13) * mm});
            skLineSegment(sketch, "E262", {"start": v(341.38, 28.8) * mm, "end": v(341.38, 60.13) * mm});
            skLineSegment(sketch, "E263.bottom", {"start": v(313.26, 344.06) * mm, "end": v(332.95, 344.06) * mm});
            skLineSegment(sketch, "E263.top", {"start": v(313.26, 335.06) * mm, "end": v(332.95, 335.06) * mm});
            skLineSegment(sketch, "E263.left", {"start": v(313.26, 344.06) * mm, "end": v(313.26, 335.06) * mm});
            skLineSegment(sketch, "E263.right", {"start": v(332.95, 344.06) * mm, "end": v(332.95, 335.06) * mm});
            skLineSegment(sketch, "E264.bottom", {"start": v(332.95, 341.06) * mm, "end": v(338.03, 341.06) * mm});
            skLineSegment(sketch, "E264.top", {"start": v(332.95, 338.06) * mm, "end": v(338.03, 338.06) * mm});
            skLineSegment(sketch, "E264.left", {"start": v(332.95, 341.06) * mm, "end": v(332.95, 338.06) * mm});
            skLineSegment(sketch, "E264.right", {"start": v(338.03, 341.06) * mm, "end": v(338.03, 338.06) * mm});
            skLineSegment(sketch, "E265", {"start": v(323.1, 335.06) * mm, "end": v(323.1, 344.06) * mm, "construction": true});
            skLineSegment(sketch, "E266.MirrorCS", {"start": v(313.26, 341.06) * mm, "end": v(308.18, 341.06) * mm});
            skLineSegment(sketch, "E267.MirrorCS", {"start": v(308.18, 341.06) * mm, "end": v(308.18, 338.06) * mm});
            skLineSegment(sketch, "E268.MirrorCS", {"start": v(313.26, 338.06) * mm, "end": v(308.18, 338.06) * mm});
            skLineSegment(sketch, "E269.bottom", {"start": v(348.4, 66.13) * mm, "end": v(343.32, 66.13) * mm});
            skLineSegment(sketch, "E269.top", {"start": v(348.4, 63.13) * mm, "end": v(343.32, 63.13) * mm});
            skLineSegment(sketch, "E269.left", {"start": v(348.4, 66.13) * mm, "end": v(348.4, 63.13) * mm});
            skLineSegment(sketch, "E269.right", {"start": v(343.32, 66.13) * mm, "end": v(343.32, 63.13) * mm});
            skPoint(sketch, "E269.middle", {"position": v(345.86, 64.63) * mm});
            skPoint(sketch, "E269.middle.positionSnap0", {"position": v(345.86, 69.13) * mm});
            skPoint(sketch, "E269.centerSnap0", {"position": v(345.86, 69.13) * mm});
            skLineSegment(sketch, "E270", {"start": v(359.08, 60) * mm, "end": v(361.41, 55.5) * mm});
            skLineSegment(sketch, "E271", {"start": v(361.41, 55.5) * mm, "end": v(364.08, 56.87) * mm});
            skLineSegment(sketch, "E272", {"start": v(364.08, 56.87) * mm, "end": v(361.74, 61.38) * mm});
            skLineSegment(sketch, "E273", {"start": v(361.74, 61.38) * mm, "end": v(359.08, 60) * mm});
            skLineSegment(sketch, "E274", {"start": v(330.61, 69.13) * mm, "end": v(279.22, 33.66) * mm});
            skLineSegment(sketch, "E275", {"start": v(294.82, 33.5) * mm, "end": v(333.42, 60.13) * mm});
            skLineSegment(sketch, "E276", {"start": v(279.22, 33.66) * mm, "end": v(311.72, 10.2) * mm});
            skLineSegment(sketch, "E277", {"start": v(294.82, 33.5) * mm, "end": v(313.67, 19.9) * mm});
            skLineSegment(sketch, "E278", {"start": v(318.08, 56.84) * mm, "end": v(322.26, 59.72) * mm});
            skLineSegment(sketch, "E279", {"start": v(322.26, 59.72) * mm, "end": v(323.97, 57.26) * mm});
            skLineSegment(sketch, "E280", {"start": v(323.97, 57.26) * mm, "end": v(319.79, 54.37) * mm});
            skLineSegment(sketch, "E281", {"start": v(319.79, 54.37) * mm, "end": v(318.08, 56.84) * mm});
            skLineSegment(sketch, "E282", {"start": v(341.38, 33.82) * mm, "end": v(311.38, 44.93) * mm});
            skLineSegment(sketch, "E283", {"start": v(341.38, 43.42) * mm, "end": v(320.43, 51.17) * mm});
            skLineSegment(sketch, "E284.bottom", {"start": v(264.14, 128.44) * mm, "end": v(260.14, 128.44) * mm});
            skLineSegment(sketch, "E284.top", {"start": v(264.14, 123.36) * mm, "end": v(260.14, 123.36) * mm});
            skLineSegment(sketch, "E284.left", {"start": v(264.14, 128.44) * mm, "end": v(264.14, 123.36) * mm});
            skLineSegment(sketch, "E284.right", {"start": v(260.14, 128.44) * mm, "end": v(260.14, 123.36) * mm});
            skPoint(sketch, "E284.middle", {"position": v(262.14, 125.9) * mm});
            skPoint(sketch, "E284.middle.positionSnap0", {"position": v(262.14, 138.44) * mm});
            skPoint(sketch, "E284.centerSnap0", {"position": v(262.14, 138.44) * mm});
            skPoint(sketch, "E285.middle", {"position": v(330.72, 21.36) * mm});
            skLineSegment(sketch, "E286.bottom", {"start": v(610.76, 241.18) * mm, "end": v(641.26, 241.18) * mm});
            skLineSegment(sketch, "E286.top", {"start": v(610.76, 232.18) * mm, "end": v(641.26, 232.18) * mm});
            skLineSegment(sketch, "E286.left", {"start": v(610.76, 241.18) * mm, "end": v(610.76, 232.18) * mm});
            skLineSegment(sketch, "E286.right", {"start": v(641.26, 241.18) * mm, "end": v(641.26, 232.18) * mm});
            skCircle(sketch, "E287", {"center": v(617.26, 236.68) * mm, "radius": 1.5 * mm});
            skPoint(sketch, "E287.centerSnap0", {"position": v(610.76, 236.68) * mm});
            skCircle(sketch, "E288", {"center": v(634.76, 236.68) * mm, "radius": 1.5 * mm});
            skPoint(sketch, "E288.centerSnap0", {"position": v(641.26, 236.68) * mm});
            skLineSegment(sketch, "E289", {"start": v(634.76, 236.68) * mm, "end": v(645.14, 204.43) * mm, "construction": true});
            skCircle(sketch, "E290", {"center": v(645.14, 204.43) * mm, "radius": 2.25 * mm});
            skLineSegment(sketch, "E291", {"start": v(645.14, 204.43) * mm, "end": v(596.59, 188.81) * mm, "construction": true});
            skCircle(sketch, "E292", {"center": v(596.59, 188.81) * mm, "radius": 1.5 * mm});
            skLineSegment(sketch, "E293", {"start": v(589.23, 190.46) * mm, "end": v(591.87, 182.25) * mm});
            skLineSegment(sketch, "E294", {"start": v(591.87, 182.25) * mm, "end": v(653.5, 202.08) * mm});
            skLineSegment(sketch, "E295", {"start": v(653.5, 202.08) * mm, "end": v(650.87, 210.3) * mm});
            skLineSegment(sketch, "E296", {"start": v(650.87, 210.3) * mm, "end": v(589.23, 190.46) * mm});
            skLineSegment(sketch, "E297", {"start": v(641.26, 241.18) * mm, "end": v(660.36, 204.28) * mm});
            skLineSegment(sketch, "E298", {"start": v(660.36, 204.28) * mm, "end": v(653.5, 202.08) * mm});
            skLineSegment(sketch, "E299", {"start": v(647.65, 209.26) * mm, "end": v(635.79, 232.18) * mm});
            skLineSegment(sketch, "E300", {"start": v(589.23, 190.46) * mm, "end": v(584.77, 179.96) * mm});
            skLineSegment(sketch, "E301", {"start": v(584.77, 179.96) * mm, "end": v(591.87, 182.25) * mm});
            skLineSegment(sketch, "E302", {"start": v(626.03, 202.3) * mm, "end": v(626.03, 232.18) * mm});
            skPoint(sketch, "E303.middle", {"position": v(626.03, 204.43) * mm});
            skLineSegment(sketch, "E304", {"start": v(630.53, 203.75) * mm, "end": v(630.53, 232.18) * mm});
            skLineSegment(sketch, "E305", {"start": v(621.53, 200.86) * mm, "end": v(621.53, 232.18) * mm});
            skLineSegment(sketch, "E306.bottom", {"start": v(628.55, 238.18) * mm, "end": v(623.47, 238.18) * mm});
            skLineSegment(sketch, "E306.top", {"start": v(628.55, 235.18) * mm, "end": v(623.47, 235.18) * mm});
            skLineSegment(sketch, "E306.left", {"start": v(628.55, 238.18) * mm, "end": v(628.55, 235.18) * mm});
            skLineSegment(sketch, "E306.right", {"start": v(623.47, 238.18) * mm, "end": v(623.47, 235.18) * mm});
            skPoint(sketch, "E306.middle", {"position": v(626.01, 236.68) * mm});
            skPoint(sketch, "E306.middle.positionSnap0", {"position": v(626.01, 241.18) * mm});
            skPoint(sketch, "E306.centerSnap0", {"position": v(626.01, 241.18) * mm});
            skLineSegment(sketch, "E307", {"start": v(639.23, 232.05) * mm, "end": v(641.56, 227.54) * mm});
            skLineSegment(sketch, "E308", {"start": v(641.56, 227.54) * mm, "end": v(644.23, 228.92) * mm});
            skLineSegment(sketch, "E309", {"start": v(644.23, 228.92) * mm, "end": v(641.9, 233.43) * mm});
            skLineSegment(sketch, "E310", {"start": v(641.9, 233.43) * mm, "end": v(639.23, 232.05) * mm});
            skLineSegment(sketch, "E311", {"start": v(610.76, 241.18) * mm, "end": v(559.37, 205.71) * mm});
            skLineSegment(sketch, "E312", {"start": v(574.97, 205.55) * mm, "end": v(613.57, 232.18) * mm});
            skLineSegment(sketch, "E313", {"start": v(559.37, 205.71) * mm, "end": v(591.87, 182.25) * mm});
            skLineSegment(sketch, "E314", {"start": v(574.97, 205.55) * mm, "end": v(593.82, 191.94) * mm});
            skLineSegment(sketch, "E315", {"start": v(598.23, 228.89) * mm, "end": v(602.41, 231.77) * mm});
            skLineSegment(sketch, "E316", {"start": v(602.41, 231.77) * mm, "end": v(604.12, 229.3) * mm});
            skLineSegment(sketch, "E317", {"start": v(604.12, 229.3) * mm, "end": v(599.94, 226.42) * mm});
            skLineSegment(sketch, "E318", {"start": v(599.94, 226.42) * mm, "end": v(598.23, 228.89) * mm});
            skLineSegment(sketch, "E319", {"start": v(621.53, 205.87) * mm, "end": v(591.53, 216.97) * mm});
            skLineSegment(sketch, "E320", {"start": v(621.53, 215.47) * mm, "end": v(600.58, 223.22) * mm});
            skPoint(sketch, "E321.middle", {"position": v(610.87, 193.4) * mm});
            skLineSegment(sketch, "E322", {"start": v(42.75, -18.86) * mm, "end": v(75.3, -18.86) * mm});
            skLineSegment(sketch, "E323", {"start": v(42.75, -18.86) * mm, "end": v(32.35, -30.61) * mm});
            skLineSegment(sketch, "E324", {"start": v(75.3, -18.86) * mm, "end": v(85.7, -30.61) * mm});
            skLineSegment(sketch, "E325", {"start": v(32.35, -30.61) * mm, "end": v(75.3, -18.86) * mm, "construction": true});
            skLineSegment(sketch, "E326", {"start": v(34.17, -28.56) * mm, "end": v(69.62, -18.86) * mm});
            skLineSegment(sketch, "E327", {"start": v(38.04, -30.61) * mm, "end": v(76.41, -20.11) * mm});
            skLineSegment(sketch, "E328", {"start": v(42.75, -9.86) * mm, "end": v(24.39, -30.61) * mm});
            skLineSegment(sketch, "E329", {"start": v(50.28, -14.36) * mm, "end": v(67.78, -14.36) * mm});
            skLineSegment(sketch, "E330", {"start": v(59.03, -18.86) * mm, "end": v(59.03, -30.61) * mm, "construction": true});
            skLineSegment(sketch, "E331.MirrorCS", {"start": v(83.89, -28.56) * mm, "end": v(48.44, -18.86) * mm});
            skLineSegment(sketch, "E332.MirrorCS", {"start": v(85.7, -30.61) * mm, "end": v(42.75, -18.86) * mm, "construction": true});
            skLineSegment(sketch, "E333.MirrorCS", {"start": v(80.02, -30.61) * mm, "end": v(41.64, -20.11) * mm});
            skLineSegment(sketch, "E334.bottom", {"start": v(85.53, -36.61) * mm, "end": v(23.81, -36.61) * mm});
            skLineSegment(sketch, "E334.top", {"start": v(85.53, -56.61) * mm, "end": v(23.81, -56.61) * mm});
            skLineSegment(sketch, "E334.left", {"start": v(85.53, -36.61) * mm, "end": v(85.53, -56.61) * mm});
            skLineSegment(sketch, "E334.right", {"start": v(23.81, -36.61) * mm, "end": v(23.81, -56.61) * mm});
            skLineSegment(sketch, "E335.bottom", {"start": v(32.94, -36.61) * mm, "end": v(37.94, -36.61) * mm});
            skLineSegment(sketch, "E335.top", {"start": v(32.94, -56.61) * mm, "end": v(37.94, -56.61) * mm});
            skLineSegment(sketch, "E335.left", {"start": v(32.94, -36.61) * mm, "end": v(32.94, -56.61) * mm});
            skLineSegment(sketch, "E335.right", {"start": v(37.94, -36.61) * mm, "end": v(37.94, -56.61) * mm});
            skLineSegment(sketch, "E336.bottom", {"start": v(47.06, -36.61) * mm, "end": v(52.06, -36.61) * mm});
            skLineSegment(sketch, "E336.top", {"start": v(47.06, -56.61) * mm, "end": v(52.06, -56.61) * mm});
            skLineSegment(sketch, "E336.left", {"start": v(47.06, -36.61) * mm, "end": v(47.06, -56.61) * mm});
            skLineSegment(sketch, "E336.right", {"start": v(52.06, -36.61) * mm, "end": v(52.06, -56.61) * mm});
            skLineSegment(sketch, "E337.bottom", {"start": v(61.18, -36.61) * mm, "end": v(66.18, -36.61) * mm});
            skLineSegment(sketch, "E337.top", {"start": v(61.18, -56.61) * mm, "end": v(66.18, -56.61) * mm});
            skLineSegment(sketch, "E337.left", {"start": v(61.18, -36.61) * mm, "end": v(61.18, -56.61) * mm});
            skLineSegment(sketch, "E337.right", {"start": v(66.18, -36.61) * mm, "end": v(66.18, -56.61) * mm});
            skLineSegment(sketch, "E338.bottom", {"start": v(75.3, -36.61) * mm, "end": v(80.3, -36.61) * mm});
            skLineSegment(sketch, "E338.top", {"start": v(75.3, -56.61) * mm, "end": v(80.3, -56.61) * mm});
            skLineSegment(sketch, "E338.left", {"start": v(75.3, -36.61) * mm, "end": v(75.3, -56.61) * mm});
            skLineSegment(sketch, "E338.right", {"start": v(80.3, -36.61) * mm, "end": v(80.3, -56.61) * mm});
            skLineSegment(sketch, "E339.bottom", {"start": v(33.23, 52.18) * mm, "end": v(28.23, 52.18) * mm});
            skLineSegment(sketch, "E339.top", {"start": v(33.23, 32.18) * mm, "end": v(28.23, 32.18) * mm});
            skLineSegment(sketch, "E339.left", {"start": v(33.23, 52.18) * mm, "end": v(33.23, 32.18) * mm});
            skLineSegment(sketch, "E339.right", {"start": v(28.23, 52.18) * mm, "end": v(28.23, 32.18) * mm});
            skPoint(sketch, "E339.middle", {"position": v(30.73, 42.18) * mm});
            skLineSegment(sketch, "E340.MirrorCS", {"start": v(41.73, 52.18) * mm, "end": v(41.73, 32.18) * mm});
            skLineSegment(sketch, "E341.MirrorCS", {"start": v(41.73, 52.18) * mm, "end": v(46.73, 52.18) * mm});
            skLineSegment(sketch, "E342.MirrorCS", {"start": v(46.73, 52.18) * mm, "end": v(46.73, 32.18) * mm});
            skLineSegment(sketch, "E343.MirrorCS", {"start": v(41.73, 32.18) * mm, "end": v(46.73, 32.18) * mm});
            skSolve(sketch);
        }
        {
            var Q0;
            Q0=makeQuery(id+"F0.imprint","IMPRINT",FACE,{"disambiguationData":[TD([[makeQuery(id+"F0.imprint","IMPRINT",EDGE,{"derivedFrom":sQuery(id+"F0.wireOp",EDGE,"E0")}),-1.0]])]});
            var Q1;
            {var subQ0=sQuery(id+"F0.wireOp",EDGE,"E10");Q1=makeQuery(id+"F0.imprint","IMPRINT",FACE,{"disambiguationData":[TD([[makeQuery(id+"F0.imprint","IMPRINT",EDGE,{"derivedFrom":subQ0}),1.0]])]});}
            var Q2;
            {var subQ0=sQuery(id+"F0.wireOp",EDGE,"E13");Q2=makeQuery(id+"F0.imprint","IMPRINT",FACE,{"disambiguationData":[TD([[makeQuery(id+"F0.imprint","IMPRINT",EDGE,{"derivedFrom":subQ0}),1.0]])]});}
            var Q3;
            {var subQ0=sQuery(id+"F0.wireOp",EDGE,"E16");Q3=makeQuery(id+"F0.imprint","IMPRINT",FACE,{"disambiguationData":[TD([[makeQuery(id+"F0.imprint","IMPRINT",EDGE,{"derivedFrom":subQ0}),1.0]])]});}
            var Q4;
            {var subQ0=sQuery(id+"F0.wireOp",EDGE,"E19");Q4=makeQuery(id+"F0.imprint","IMPRINT",FACE,{"disambiguationData":[TD([[makeQuery(id+"F0.imprint","IMPRINT",EDGE,{"derivedFrom":subQ0}),1.0]])]});}
            var Q5;
            {var subQ0=sQuery(id+"F0.wireOp",EDGE,"E2.MirrorCS");Q5=makeQuery(id+"F0.imprint","IMPRINT",FACE,{"disambiguationData":[TD([[makeQuery(id+"F0.imprint","IMPRINT",EDGE,{"derivedFrom":subQ0}),-1.0]])]});}
            var Q6;
            {var subQ0=sQuery(id+"F0.wireOp",EDGE,"E5.MirrorCS");Q6=makeQuery(id+"F0.imprint","IMPRINT",FACE,{"disambiguationData":[TD([[makeQuery(id+"F0.imprint","IMPRINT",EDGE,{"derivedFrom":subQ0}),1.0]])]});}
            var Q7;
            {var subQ5=sQuery(id+"F0.wireOp",EDGE,"E41.left");Q7=makeQuery(id+"F0.imprint","IMPRINT",FACE,{"disambiguationData":[TD([[makeQuery(id+"F0.imprint","IMPRINT",EDGE,{"derivedFrom":subQ5}),-1.0]])]});}
            var Q8;
            Q8=makeQuery(id+"F0.imprint","IMPRINT",FACE,{"disambiguationData":[TD([[makeQuery(id+"F0.imprint","IMPRINT",EDGE,{"derivedFrom":sQuery(id+"F0.wireOp",EDGE,"E58.MirrorCS")}),-1.0]])]});
            var Q9;
            Q9=makeQuery(id+"F0.imprint","IMPRINT",FACE,{"disambiguationData":[TD([[makeQuery(id+"F0.imprint","IMPRINT",EDGE,{"derivedFrom":sQuery(id+"F0.wireOp",EDGE,"E64.MirrorCS")}),-1.0]])]});
            var Q10;
            Q10=makeQuery(id+"F0.imprint","IMPRINT",FACE,{"disambiguationData":[TD([[makeQuery(id+"F0.imprint","IMPRINT",EDGE,{"derivedFrom":sQuery(id+"F0.wireOp",EDGE,"E67.MirrorCS")}),-1.0]])]});
            var Q11;
            {var subQ2=sQuery(id+"F0.wireOp",EDGE,"E70.MirrorCS");Q11=makeQuery(id+"F0.imprint","IMPRINT",FACE,{"disambiguationData":[TD([[makeQuery(id+"F0.imprint","IMPRINT",EDGE,{"derivedFrom":subQ2}),-1.0]])]});}
            var Q12;
            Q12=makeQuery(id+"F0.imprint","IMPRINT",FACE,{"disambiguationData":[TD([[makeQuery(id+"F0.imprint","IMPRINT",EDGE,{"derivedFrom":sQuery(id+"F0.wireOp",EDGE,"E41.bottom")}),-1.0]])]});
            var Q13;
            {var subQ0=sQuery(id+"F0.wireOp",EDGE,"E73.MirrorCS");Q13=makeQuery(id+"F0.imprint","IMPRINT",FACE,{"disambiguationData":[TD([[makeQuery(id+"F0.imprint","IMPRINT",EDGE,{"derivedFrom":subQ0}),-1.0]])]});}
            var Q14;
            {var subQ2=sQuery(id+"F0.wireOp",EDGE,"E54");Q14=makeQuery(id+"F0.imprint","IMPRINT",FACE,{"disambiguationData":[TD([[makeQuery(id+"F0.imprint","IMPRINT",EDGE,{"derivedFrom":subQ2}),1.0]])]});}
            var Q15;
            {var subQ0=sQuery(id+"F0.wireOp",EDGE,"E51");Q15=makeQuery(id+"F0.imprint","IMPRINT",FACE,{"disambiguationData":[TD([[makeQuery(id+"F0.imprint","IMPRINT",EDGE,{"derivedFrom":subQ0}),1.0]])]});}
            var Q16;
            {var subQ0=sQuery(id+"F0.wireOp",EDGE,"E48");Q16=makeQuery(id+"F0.imprint","IMPRINT",FACE,{"disambiguationData":[TD([[makeQuery(id+"F0.imprint","IMPRINT",EDGE,{"derivedFrom":subQ0}),1.0]])]});}
            var Q17;
            {var subQ0=sQuery(id+"F0.wireOp",EDGE,"E45");Q17=makeQuery(id+"F0.imprint","IMPRINT",FACE,{"disambiguationData":[TD([[makeQuery(id+"F0.imprint","IMPRINT",EDGE,{"derivedFrom":subQ0}),1.0]])]});}
            var Q18;
            {var subQ0=sQuery(id+"F0.wireOp",EDGE,"E42");Q18=makeQuery(id+"F0.imprint","IMPRINT",FACE,{"disambiguationData":[TD([[makeQuery(id+"F0.imprint","IMPRINT",EDGE,{"derivedFrom":subQ0}),1.0]])]});}
            var Q19;
            {var subQ4=sQuery(id+"F0.wireOp",EDGE,"E61.MirrorCS");Q19=makeQuery(id+"F0.imprint","IMPRINT",FACE,{"disambiguationData":[TD([[makeQuery(id+"F0.imprint","IMPRINT",EDGE,{"derivedFrom":subQ4}),-1.0]])]});}
            var Q20;
            {var subQ0=sQuery(id+"F0.wireOp",EDGE,"E130.MirrorCS");Q20=makeQuery(id+"F0.imprint","IMPRINT",FACE,{"disambiguationData":[TD([[makeQuery(id+"F0.imprint","IMPRINT",EDGE,{"derivedFrom":subQ0}),1.0]])]});}
            var Q21;
            {var subQ2=sQuery(id+"F0.wireOp",EDGE,"E120.MirrorCS");Q21=makeQuery(id+"F0.imprint","IMPRINT",FACE,{"disambiguationData":[TD([[makeQuery(id+"F0.imprint","IMPRINT",EDGE,{"derivedFrom":subQ2}),1.0]])]});}
            var Q22;
            {var subQ16=sQuery(id+"F0.wireOp",EDGE,"E107.bottom");Q22=makeQuery(id+"F0.imprint","IMPRINT",FACE,{"disambiguationData":[TD([[makeQuery(id+"F0.imprint","IMPRINT",EDGE,{"derivedFrom":subQ16}),1.0]])]});}
            var Q23;
            {var subQ1=sQuery(id+"F0.wireOp",EDGE,"01f4eec0-e44f-4571-a178-ea1639a5797c.right");var subQ7=sQuery(id+"F0.wireOp",EDGE,"01f4eec0-e44f-4571-a178-ea1639a5797c.top");var subQ8=makeQuery(id+"F0.imprint","INTERSECT",VERTEX,{"derivedFrom":[subQ7,subQ1]});Q23=makeQuery(id+"F0.imprint","IMPRINT",FACE,{"disambiguationData":[TD([[makeQuery(id+"F0.imprint","IMPRINT",EDGE,{"disambiguationData":[TD([[subQ8,1.0]])],"derivedFrom":subQ7}),-1.0]])]});}
            var Q24;
            {var subQ2=sQuery(id+"F0.wireOp",EDGE,"E129.MirrorCS");Q24=makeQuery(id+"F0.imprint","IMPRINT",FACE,{"disambiguationData":[TD([[makeQuery(id+"F0.imprint","IMPRINT",EDGE,{"derivedFrom":subQ2}),-1.0]])]});}
            var Q25;
            {var subQ0=sQuery(id+"F0.wireOp",EDGE,"E109");Q25=makeQuery(id+"F0.imprint","IMPRINT",FACE,{"disambiguationData":[TD([[makeQuery(id+"F0.imprint","IMPRINT",EDGE,{"derivedFrom":subQ0}),1.0]])]});}
            var Q26;
            {var subQ1=sQuery(id+"F0.wireOp",EDGE,"E112");Q26=makeQuery(id+"F0.imprint","IMPRINT",FACE,{"disambiguationData":[TD([[makeQuery(id+"F0.imprint","IMPRINT",EDGE,{"derivedFrom":subQ1}),-1.0]])]});}
            var Q27;
            {var subQ0=sQuery(id+"F0.wireOp",EDGE,"E126.MirrorCS");Q27=makeQuery(id+"F0.imprint","IMPRINT",FACE,{"disambiguationData":[TD([[makeQuery(id+"F0.imprint","IMPRINT",EDGE,{"derivedFrom":subQ0}),1.0]])]});}
            var Q28;
            {var subQ0=sQuery(id+"F0.wireOp",EDGE,"E123.MirrorCS");Q28=makeQuery(id+"F0.imprint","IMPRINT",FACE,{"disambiguationData":[TD([[makeQuery(id+"F0.imprint","IMPRINT",EDGE,{"derivedFrom":subQ0}),1.0]])]});}
            var Q29;
            {var subQ0=sQuery(id+"F0.wireOp",EDGE,"E113");Q29=makeQuery(id+"F0.imprint","IMPRINT",FACE,{"disambiguationData":[TD([[makeQuery(id+"F0.imprint","IMPRINT",EDGE,{"derivedFrom":subQ0}),-1.0]])]});}
            var Q30;
            {var subQ0=sQuery(id+"F0.wireOp",EDGE,"E116");Q30=makeQuery(id+"F0.imprint","IMPRINT",FACE,{"disambiguationData":[TD([[makeQuery(id+"F0.imprint","IMPRINT",EDGE,{"derivedFrom":subQ0}),-1.0]])]});}
            var Q31;
            {var subQ0=sQuery(id+"F0.wireOp",EDGE,"6f9e3fd8-1ead-4cb0-8138-0493278e9d39");var subQ1=sQuery(id+"F0.wireOp",EDGE,"fc38524c-97cf-4899-b48e-28cbca903469");var subQ2=makeQuery(id+"F0.imprint","INTERSECT",VERTEX,{"derivedFrom":[subQ1,subQ0]});Q31=makeQuery(id+"F0.imprint","IMPRINT",FACE,{"disambiguationData":[TD([[makeQuery(id+"F0.imprint","IMPRINT",EDGE,{"disambiguationData":[TD([[subQ2,-1.0]])],"derivedFrom":subQ1}),-1.0]])]});}
            var Q32;
            {var subQ5=sQuery(id+"F0.wireOp",EDGE,"01f4eec0-e44f-4571-a178-ea1639a5797c.left");var subQ6=sQuery(id+"F0.wireOp",EDGE,"01f4eec0-e44f-4571-a178-ea1639a5797c.bottom");var subQ7=makeQuery(id+"F0.imprint","INTERSECT",VERTEX,{"derivedFrom":[subQ6,subQ5]});Q32=makeQuery(id+"F0.imprint","IMPRINT",FACE,{"disambiguationData":[TD([[makeQuery(id+"F0.imprint","IMPRINT",EDGE,{"disambiguationData":[TD([[subQ7,-1.0]])],"derivedFrom":subQ6}),1.0]])]});}
            var Q33;
            {var subQ1=sQuery(id+"F0.wireOp",EDGE,"01f4eec0-e44f-4571-a178-ea1639a5797c.top");var subQ6=sQuery(id+"F0.wireOp",EDGE,"01f4eec0-e44f-4571-a178-ea1639a5797c.left");var subQ9=makeQuery(id+"F0.imprint","INTERSECT",VERTEX,{"derivedFrom":[subQ1,subQ6]});Q33=makeQuery(id+"F0.imprint","IMPRINT",FACE,{"disambiguationData":[TD([[makeQuery(id+"F0.imprint","IMPRINT",EDGE,{"disambiguationData":[TD([[subQ9,-1.0]])],"derivedFrom":subQ1}),-1.0]])]});}
            var Q34;
            {var subQ1=sQuery(id+"F0.wireOp",EDGE,"01f4eec0-e44f-4571-a178-ea1639a5797c.right");var subQ5=sQuery(id+"F0.wireOp",EDGE,"01f4eec0-e44f-4571-a178-ea1639a5797c.bottom");var subQ6=makeQuery(id+"F0.imprint","INTERSECT",VERTEX,{"derivedFrom":[subQ5,subQ1]});Q34=makeQuery(id+"F0.imprint","IMPRINT",FACE,{"disambiguationData":[TD([[makeQuery(id+"F0.imprint","IMPRINT",EDGE,{"disambiguationData":[TD([[subQ6,1.0]])],"derivedFrom":subQ5}),1.0]])]});}
            var Q35;
            Q35=makeQuery(id+"F0.imprint","IMPRINT",FACE,{"disambiguationData":[TD([[makeQuery(id+"F0.imprint","IMPRINT",EDGE,{"derivedFrom":sQuery(id+"F0.wireOp",EDGE,"E78.MirrorCS")}),-1.0]])]});
            var Q36;
            {var subQ0=sQuery(id+"F0.wireOp",EDGE,"E84");Q36=makeQuery(id+"F0.imprint","IMPRINT",FACE,{"disambiguationData":[TD([[makeQuery(id+"F0.imprint","IMPRINT",EDGE,{"derivedFrom":subQ0}),1.0]])]});}
            var Q37;
            {var subQ22=sQuery(id+"F0.wireOp",EDGE,"E99.left");Q37=makeQuery(id+"F0.imprint","IMPRINT",FACE,{"disambiguationData":[TD([[makeQuery(id+"F0.imprint","IMPRINT",EDGE,{"derivedFrom":subQ22}),-1.0]])]});}
            var Q38;
            Q38=makeQuery(id+"F0.imprint","IMPRINT",FACE,{"disambiguationData":[TD([[makeQuery(id+"F0.imprint","IMPRINT",EDGE,{"derivedFrom":sQuery(id+"F0.wireOp",EDGE,"E100.bottom")}),1.0]])]});
            var Q39;
            {var subQ0=sQuery(id+"F0.wireOp",EDGE,"E90");Q39=makeQuery(id+"F0.imprint","IMPRINT",FACE,{"disambiguationData":[TD([[makeQuery(id+"F0.imprint","IMPRINT",EDGE,{"derivedFrom":subQ0}),1.0]])]});}
            var Q40;
            {var subQ1=sQuery(id+"F0.wireOp",EDGE,"E100.right");Q40=makeQuery(id+"F0.imprint","IMPRINT",FACE,{"disambiguationData":[TD([[makeQuery(id+"F0.imprint","IMPRINT",EDGE,{"derivedFrom":subQ1}),-1.0]])]});}
            var Q41;
            {var subQ1=sQuery(id+"F0.wireOp",EDGE,"E100.left");Q41=makeQuery(id+"F0.imprint","IMPRINT",FACE,{"disambiguationData":[TD([[makeQuery(id+"F0.imprint","IMPRINT",EDGE,{"derivedFrom":subQ1}),1.0]])]});}
            var Q42;
            Q42=makeQuery(id+"F0.imprint","IMPRINT",FACE,{"disambiguationData":[TD([[makeQuery(id+"F0.imprint","IMPRINT",EDGE,{"derivedFrom":sQuery(id+"F0.wireOp",EDGE,"E79.MirrorCS")}),1.0]])]});
            var Q43;
            {var subQ0=sQuery(id+"F0.wireOp",EDGE,"E87");Q43=makeQuery(id+"F0.imprint","IMPRINT",FACE,{"disambiguationData":[TD([[makeQuery(id+"F0.imprint","IMPRINT",EDGE,{"derivedFrom":subQ0}),1.0]])]});}
            var Q44;
            {var subQ0=sQuery(id+"F0.wireOp",EDGE,"E81");Q44=makeQuery(id+"F0.imprint","IMPRINT",FACE,{"disambiguationData":[TD([[makeQuery(id+"F0.imprint","IMPRINT",EDGE,{"derivedFrom":subQ0}),1.0]])]});}
            var Q45;
            {var subQ0=sQuery(id+"F0.wireOp",EDGE,"E326");var subQ1=sQuery(id+"F0.wireOp",EDGE,"E322");var subQ2=makeQuery(id+"F0.imprint","INTERSECT",VERTEX,{"derivedFrom":[subQ1,subQ0]});Q45=makeQuery(id+"F0.imprint","IMPRINT",FACE,{"disambiguationData":[TD([[makeQuery(id+"F0.imprint","IMPRINT",EDGE,{"disambiguationData":[TD([[subQ2,1.0]])],"derivedFrom":subQ0}),-1.0]])]});}
            var Q46;
            {var subQ0=sQuery(id+"F0.wireOp",EDGE,"E331.MirrorCS");var subQ1=sQuery(id+"F0.wireOp",EDGE,"E104");var subQ2=makeQuery(id+"F0.imprint","INTERSECT",VERTEX,{"derivedFrom":[subQ1,subQ0]});Q46=makeQuery(id+"F0.imprint","IMPRINT",FACE,{"disambiguationData":[TD([[makeQuery(id+"F0.imprint","IMPRINT",EDGE,{"disambiguationData":[TD([[subQ2,-1.0]])],"derivedFrom":subQ1}),-1.0]])]});}
            var Q47;
            {var subQ0=sQuery(id+"F0.wireOp",EDGE,"E326");var subQ1=sQuery(id+"F0.wireOp",EDGE,"E103");var subQ2=makeQuery(id+"F0.imprint","INTERSECT",VERTEX,{"derivedFrom":[subQ1,subQ0]});Q47=makeQuery(id+"F0.imprint","IMPRINT",FACE,{"disambiguationData":[TD([[makeQuery(id+"F0.imprint","IMPRINT",EDGE,{"disambiguationData":[TD([[subQ2,-1.0]])],"derivedFrom":subQ1}),1.0]])]});}
            var Q48;
            {var subQ0=sQuery(id+"F0.wireOp",EDGE,"E333.MirrorCS");var subQ1=sQuery(id+"F0.wireOp",EDGE,"E326");var subQ2=makeQuery(id+"F0.imprint","INTERSECT",VERTEX,{"derivedFrom":[subQ1,subQ0]});Q48=makeQuery(id+"F0.imprint","IMPRINT",FACE,{"disambiguationData":[TD([[makeQuery(id+"F0.imprint","IMPRINT",EDGE,{"disambiguationData":[TD([[subQ2,-1.0]])],"derivedFrom":subQ1}),-1.0]])]});}
            var Q49;
            {var subQ0=sQuery(id+"F0.wireOp",EDGE,"E333.MirrorCS");var subQ1=sQuery(id+"F0.wireOp",EDGE,"E326");var subQ2=makeQuery(id+"F0.imprint","INTERSECT",VERTEX,{"derivedFrom":[subQ1,subQ0]});Q49=makeQuery(id+"F0.imprint","IMPRINT",FACE,{"disambiguationData":[TD([[makeQuery(id+"F0.imprint","IMPRINT",EDGE,{"disambiguationData":[TD([[subQ2,-1.0]])],"derivedFrom":subQ1}),1.0]])]});}
            var Q50;
            {var subQ0=sQuery(id+"F0.wireOp",EDGE,"E323");var subQ1=sQuery(id+"F0.wireOp",EDGE,"E93");var subQ2=makeQuery(id+"F0.imprint","INTERSECT",VERTEX,{"derivedFrom":[subQ1,subQ0]});Q50=makeQuery(id+"F0.imprint","IMPRINT",FACE,{"disambiguationData":[TD([[makeQuery(id+"F0.imprint","IMPRINT",EDGE,{"disambiguationData":[TD([[subQ2,-1.0]])],"derivedFrom":subQ1}),1.0]])]});}
            var Q51;
            {var subQ1=sQuery(id+"F0.wireOp",EDGE,"E324");var subQ5=sQuery(id+"F0.wireOp",EDGE,"E93");var subQ6=makeQuery(id+"F0.imprint","INTERSECT",VERTEX,{"derivedFrom":[subQ5,subQ1]});Q51=makeQuery(id+"F0.imprint","IMPRINT",FACE,{"disambiguationData":[TD([[makeQuery(id+"F0.imprint","IMPRINT",EDGE,{"disambiguationData":[TD([[subQ6,1.0]])],"derivedFrom":subQ5}),1.0]])]});}
            var Q52;
            {var subQ0=sQuery(id+"F0.wireOp",EDGE,"E323");var subQ3=sQuery(id+"F0.wireOp",EDGE,"E333.MirrorCS");var subQ5=makeQuery(id+"F0.imprint","INTERSECT",VERTEX,{"derivedFrom":[subQ0,subQ3]});Q52=makeQuery(id+"F0.imprint","IMPRINT",FACE,{"disambiguationData":[TD([[makeQuery(id+"F0.imprint","IMPRINT",EDGE,{"disambiguationData":[TD([[subQ5,1.0]])],"derivedFrom":subQ3}),-1.0]])]});}
            var Q53;
            {var subQ0=sQuery(id+"F0.wireOp",EDGE,"E324");var subQ3=sQuery(id+"F0.wireOp",EDGE,"E327");var subQ5=makeQuery(id+"F0.imprint","INTERSECT",VERTEX,{"derivedFrom":[subQ0,subQ3]});Q53=makeQuery(id+"F0.imprint","IMPRINT",FACE,{"disambiguationData":[TD([[makeQuery(id+"F0.imprint","IMPRINT",EDGE,{"disambiguationData":[TD([[subQ5,1.0]])],"derivedFrom":subQ3}),1.0]])]});}
            var Q54;
            Q54=makeQuery(id+"F0.imprint","IMPRINT",FACE,{"disambiguationData":[TD([[makeQuery(id+"F0.imprint","IMPRINT",EDGE,{"derivedFrom":sQuery(id+"F0.wireOp",EDGE,"E334.bottom")}),1.0]])]});
            extrude(context, id + "F1", {"entities" : qUnion([Q0, Q1, Q2, Q3, Q4, Q5, Q6, Q7, Q8, Q9, Q10, Q11, Q12, Q13, Q14, Q15, Q16, Q17, Q18, Q19, Q20, Q21, Q22, Q23, Q24, Q25, Q26, Q27, Q28, Q29, Q30, Q31, Q32, Q33, Q34, Q35, Q36, Q37, Q38, Q39, Q40, Q41, Q42, Q43, Q44, Q45, Q46, Q47, Q48, Q49, Q50, Q51, Q52, Q53, Q54]), "depth" : 3.17 * mm, "offsetDistance" : 25 * mm});
        }
        {
            var Q0;
            Q0=makeQuery(id+"F0.imprint","IMPRINT",FACE,{"disambiguationData":[TD([[makeQuery(id+"F0.imprint","IMPRINT",EDGE,{"derivedFrom":sQuery(id+"F0.wireOp",EDGE,"E141")}),-1.0]])]});
            var Q1;
            Q1=makeQuery(id+"F0.imprint","IMPRINT",FACE,{"disambiguationData":[TD([[makeQuery(id+"F0.imprint","IMPRINT",EDGE,{"derivedFrom":sQuery(id+"F0.wireOp",EDGE,"E145.top")}),-1.0]])]});
            var Q2;
            Q2=makeQuery(id+"F0.imprint","IMPRINT",FACE,{"disambiguationData":[TD([[makeQuery(id+"F0.imprint","IMPRINT",EDGE,{"derivedFrom":sQuery(id+"F0.wireOp",EDGE,"E145.right")}),-1.0]])]});
            var Q3;
            Q3=makeQuery(id+"F0.imprint","IMPRINT",FACE,{"disambiguationData":[TD([[makeQuery(id+"F0.imprint","IMPRINT",EDGE,{"derivedFrom":sQuery(id+"F0.wireOp",EDGE,"E157.bottom")}),-1.0]])]});
            var Q4;
            Q4=makeQuery(id+"F0.imprint","IMPRINT",FACE,{"disambiguationData":[TD([[makeQuery(id+"F0.imprint","IMPRINT",EDGE,{"derivedFrom":sQuery(id+"F0.wireOp",EDGE,"E160.left")}),-1.0]])]});
            var Q5;
            Q5=makeQuery(id+"F0.imprint","IMPRINT",FACE,{"disambiguationData":[TD([[makeQuery(id+"F0.imprint","IMPRINT",EDGE,{"derivedFrom":sQuery(id+"F0.wireOp",EDGE,"E160.bottom")}),-1.0]])]});
            var Q6;
            Q6=makeQuery(id+"F0.imprint","IMPRINT",FACE,{"disambiguationData":[TD([[makeQuery(id+"F0.imprint","IMPRINT",EDGE,{"derivedFrom":sQuery(id+"F0.wireOp",EDGE,"E160.right")}),1.0]])]});
            var Q7;
            Q7=makeQuery(id+"F0.imprint","IMPRINT",FACE,{"disambiguationData":[TD([[makeQuery(id+"F0.imprint","IMPRINT",EDGE,{"derivedFrom":sQuery(id+"F0.wireOp",EDGE,"E174")}),-1.0]])]});
            var Q8;
            Q8=makeQuery(id+"F0.imprint","IMPRINT",FACE,{"disambiguationData":[TD([[makeQuery(id+"F0.imprint","IMPRINT",EDGE,{"derivedFrom":sQuery(id+"F0.wireOp",EDGE,"E170.bottom")}),-1.0]])]});
            var Q9;
            Q9=makeQuery(id+"F0.imprint","IMPRINT",FACE,{"disambiguationData":[TD([[makeQuery(id+"F0.imprint","IMPRINT",EDGE,{"derivedFrom":sQuery(id+"F0.wireOp",EDGE,"upClCsko-JJGf-5to9-oWuY-VK2MvJjFc0tL.left")}),1.0]])]});
            var Q10;
            {var subQ3=sQuery(id+"F0.wireOp",EDGE,"E170.left");Q10=makeQuery(id+"F0.imprint","IMPRINT",FACE,{"disambiguationData":[TD([[makeQuery(id+"F0.imprint","IMPRINT",EDGE,{"derivedFrom":subQ3}),-1.0]])]});}
            var Q11;
            Q11=makeQuery(id+"F0.imprint","IMPRINT",FACE,{"disambiguationData":[TD([[makeQuery(id+"F0.imprint","IMPRINT",EDGE,{"derivedFrom":sQuery(id+"F0.wireOp",EDGE,"E177")}),-1.0]])]});
            var Q12;
            Q12=makeQuery(id+"F0.imprint","IMPRINT",FACE,{"disambiguationData":[TD([[makeQuery(id+"F0.imprint","IMPRINT",EDGE,{"derivedFrom":sQuery(id+"F0.wireOp",EDGE,"E186")}),-1.0]])]});
            var Q13;
            Q13=makeQuery(id+"F0.imprint","IMPRINT",FACE,{"disambiguationData":[TD([[makeQuery(id+"F0.imprint","IMPRINT",EDGE,{"derivedFrom":sQuery(id+"F0.wireOp",EDGE,"E188")}),-1.0]])]});
            var Q14;
            Q14=makeQuery(id+"F0.imprint","IMPRINT",FACE,{"disambiguationData":[TD([[makeQuery(id+"F0.imprint","IMPRINT",EDGE,{"derivedFrom":sQuery(id+"F0.wireOp",EDGE,"E190.top")}),1.0]])]});
            var Q15;
            {var subQ0=sQuery(id+"F0.wireOp",EDGE,"E193");Q15=makeQuery(id+"F0.imprint","IMPRINT",FACE,{"disambiguationData":[TD([[makeQuery(id+"F0.imprint","IMPRINT",EDGE,{"derivedFrom":subQ0}),-1.0]])]});}
            var Q16;
            {var subQ0=sQuery(id+"F0.wireOp",EDGE,"E206.MirrorCS");Q16=makeQuery(id+"F0.imprint","IMPRINT",FACE,{"disambiguationData":[TD([[makeQuery(id+"F0.imprint","IMPRINT",EDGE,{"derivedFrom":subQ0}),1.0]])]});}
            var Q17;
            {var subQ3=sQuery(id+"F0.wireOp",EDGE,"E203.bottom");Q17=makeQuery(id+"F0.imprint","IMPRINT",FACE,{"disambiguationData":[TD([[makeQuery(id+"F0.imprint","IMPRINT",EDGE,{"derivedFrom":subQ3}),-1.0]])]});}
            var Q18;
            Q18=makeQuery(id+"F0.imprint","IMPRINT",FACE,{"disambiguationData":[TD([[makeQuery(id+"F0.imprint","IMPRINT",EDGE,{"derivedFrom":sQuery(id+"F0.wireOp",EDGE,"E204.bottom")}),-1.0]])]});
            var Q19;
            Q19=makeQuery(id+"F0.imprint","IMPRINT",FACE,{"disambiguationData":[TD([[makeQuery(id+"F0.imprint","IMPRINT",EDGE,{"derivedFrom":sQuery(id+"F0.wireOp",EDGE,"E209")}),-1.0]])]});
            var Q20;
            Q20=makeQuery(id+"F0.imprint","IMPRINT",FACE,{"disambiguationData":[TD([[makeQuery(id+"F0.imprint","IMPRINT",EDGE,{"derivedFrom":sQuery(id+"F0.wireOp",EDGE,"E214")}),1.0]])]});
            var Q21;
            Q21=makeQuery(id+"F0.imprint","IMPRINT",FACE,{"disambiguationData":[TD([[makeQuery(id+"F0.imprint","IMPRINT",EDGE,{"derivedFrom":sQuery(id+"F0.wireOp",EDGE,"E219")}),-1.0]])]});
            var Q22;
            Q22=makeQuery(id+"F0.imprint","IMPRINT",FACE,{"disambiguationData":[TD([[makeQuery(id+"F0.imprint","IMPRINT",EDGE,{"derivedFrom":sQuery(id+"F0.wireOp",EDGE,"E225")}),1.0]])]});
            var Q23;
            Q23=makeQuery(id+"F0.imprint","IMPRINT",FACE,{"disambiguationData":[TD([[makeQuery(id+"F0.imprint","IMPRINT",EDGE,{"derivedFrom":sQuery(id+"F0.wireOp",EDGE,"E238.bottom")}),-1.0]])]});
            var Q24;
            Q24=makeQuery(id+"F0.imprint","IMPRINT",FACE,{"disambiguationData":[TD([[makeQuery(id+"F0.imprint","IMPRINT",EDGE,{"derivedFrom":sQuery(id+"F0.wireOp",EDGE,"E231")}),-1.0]])]});
            var Q25;
            Q25=makeQuery(id+"F0.imprint","IMPRINT",FACE,{"disambiguationData":[TD([[makeQuery(id+"F0.imprint","IMPRINT",EDGE,{"derivedFrom":sQuery(id+"F0.wireOp",EDGE,"E230")}),1.0]])]});
            var Q26;
            {var subQ0=sQuery(id+"F0.wireOp",EDGE,"E249.MirrorCS");Q26=makeQuery(id+"F0.imprint","IMPRINT",FACE,{"disambiguationData":[TD([[makeQuery(id+"F0.imprint","IMPRINT",EDGE,{"derivedFrom":subQ0}),1.0]])]});}
            var Q27;
            {var subQ3=sQuery(id+"F0.wireOp",EDGE,"E246.bottom");Q27=makeQuery(id+"F0.imprint","IMPRINT",FACE,{"disambiguationData":[TD([[makeQuery(id+"F0.imprint","IMPRINT",EDGE,{"derivedFrom":subQ3}),-1.0]])]});}
            var Q28;
            Q28=makeQuery(id+"F0.imprint","IMPRINT",FACE,{"disambiguationData":[TD([[makeQuery(id+"F0.imprint","IMPRINT",EDGE,{"derivedFrom":sQuery(id+"F0.wireOp",EDGE,"E247.bottom")}),-1.0]])]});
            var Q29;
            {var subQ0=sQuery(id+"F0.wireOp",EDGE,"tk5jJL17-5uNP-0RkL-1Pf5-jbEVMPy6H1yz");Q29=makeQuery(id+"F0.imprint","IMPRINT",FACE,{"disambiguationData":[TD([[makeQuery(id+"F0.imprint","IMPRINT",EDGE,{"derivedFrom":subQ0}),1.0]])]});}
            var Q30;
            {var subQ0=sQuery(id+"F0.wireOp",EDGE,"3a42e403-316e-48c9-baca-a09d41d94aee0.MirrorCS");Q30=makeQuery(id+"F0.imprint","IMPRINT",FACE,{"disambiguationData":[TD([[makeQuery(id+"F0.imprint","IMPRINT",EDGE,{"derivedFrom":subQ0}),-1.0]])]});}
            var Q31;
            {var subQ0=sQuery(id+"F0.wireOp",EDGE,"PRdTr2vA-inNL-2AtP-MndJ-217gAObGIG9V");Q31=makeQuery(id+"F0.imprint","IMPRINT",FACE,{"disambiguationData":[TD([[makeQuery(id+"F0.imprint","IMPRINT",EDGE,{"derivedFrom":subQ0}),-1.0]])]});}
            var Q32;
            {var subQ3=sQuery(id+"F0.wireOp",EDGE,"E253.bottom");Q32=makeQuery(id+"F0.imprint","IMPRINT",FACE,{"disambiguationData":[TD([[makeQuery(id+"F0.imprint","IMPRINT",EDGE,{"derivedFrom":subQ3}),1.0]])]});}
            var Q33;
            Q33=makeQuery(id+"F0.imprint","IMPRINT",FACE,{"disambiguationData":[TD([[makeQuery(id+"F0.imprint","IMPRINT",EDGE,{"derivedFrom":sQuery(id+"F0.wireOp",EDGE,"E254.bottom")}),-1.0]])]});
            var Q34;
            {var subQ0=sQuery(id+"F0.wireOp",EDGE,"E256.MirrorCS");Q34=makeQuery(id+"F0.imprint","IMPRINT",FACE,{"disambiguationData":[TD([[makeQuery(id+"F0.imprint","IMPRINT",EDGE,{"derivedFrom":subQ0}),1.0]])]});}
            var Q35;
            {var subQ10=sQuery(id+"F0.wireOp",EDGE,"E260.left");Q35=makeQuery(id+"F0.imprint","IMPRINT",FACE,{"disambiguationData":[TD([[makeQuery(id+"F0.imprint","IMPRINT",EDGE,{"derivedFrom":subQ10}),1.0]])]});}
            var Q36;
            {var subQ10=sQuery(id+"F0.wireOp",EDGE,"E260.right");Q36=makeQuery(id+"F0.imprint","IMPRINT",FACE,{"disambiguationData":[TD([[makeQuery(id+"F0.imprint","IMPRINT",EDGE,{"derivedFrom":subQ10}),-1.0]])]});}
            var Q37;
            {var subQ3=sQuery(id+"F0.wireOp",EDGE,"E263.bottom");Q37=makeQuery(id+"F0.imprint","IMPRINT",FACE,{"disambiguationData":[TD([[makeQuery(id+"F0.imprint","IMPRINT",EDGE,{"derivedFrom":subQ3}),-1.0]])]});}
            var Q38;
            {var subQ0=sQuery(id+"F0.wireOp",EDGE,"E266.MirrorCS");Q38=makeQuery(id+"F0.imprint","IMPRINT",FACE,{"disambiguationData":[TD([[makeQuery(id+"F0.imprint","IMPRINT",EDGE,{"derivedFrom":subQ0}),1.0]])]});}
            var Q39;
            Q39=makeQuery(id+"F0.imprint","IMPRINT",FACE,{"disambiguationData":[TD([[makeQuery(id+"F0.imprint","IMPRINT",EDGE,{"derivedFrom":sQuery(id+"F0.wireOp",EDGE,"E264.bottom")}),-1.0]])]});
            var Q40;
            {var subQ0=sQuery(id+"F0.wireOp",EDGE,"E259");var subQ1=sQuery(id+"F0.wireOp",EDGE,"E170.top");var subQ2=makeQuery(id+"F0.imprint","INTERSECT",VERTEX,{"derivedFrom":[subQ1,subQ0]});Q40=makeQuery(id+"F0.imprint","IMPRINT",FACE,{"disambiguationData":[TD([[makeQuery(id+"F0.imprint","IMPRINT",EDGE,{"disambiguationData":[TD([[subQ2,-1.0]])],"derivedFrom":subQ1}),-1.0]])]});}
            var Q41;
            {var subQ0=sQuery(id+"F0.wireOp",EDGE,"E259");var subQ1=sQuery(id+"F0.wireOp",EDGE,"E170.top");var subQ2=makeQuery(id+"F0.imprint","INTERSECT",VERTEX,{"derivedFrom":[subQ1,subQ0]});Q41=makeQuery(id+"F0.imprint","IMPRINT",FACE,{"disambiguationData":[TD([[makeQuery(id+"F0.imprint","IMPRINT",EDGE,{"disambiguationData":[TD([[subQ2,1.0]])],"derivedFrom":subQ1}),-1.0]])]});}
            var Q42;
            {var subQ9=sQuery(id+"F0.wireOp",EDGE,"E179");Q42=makeQuery(id+"F0.imprint","IMPRINT",FACE,{"disambiguationData":[TD([[makeQuery(id+"F0.imprint","IMPRINT",EDGE,{"derivedFrom":subQ9}),-1.0]])]});}
            var Q43;
            {var subQ1=sQuery(id+"F0.wireOp",EDGE,"E180");var subQ3=sQuery(id+"F0.wireOp",EDGE,"UKyjiwe6-H5K3-qQ4C-PN59-mvtJld7moLAw");var subQ4=makeQuery(id+"F0.imprint","INTERSECT",VERTEX,{"derivedFrom":[subQ1,subQ3]});Q43=makeQuery(id+"F0.imprint","IMPRINT",FACE,{"disambiguationData":[TD([[makeQuery(id+"F0.imprint","IMPRINT",EDGE,{"disambiguationData":[TD([[subQ4,1.0]])],"derivedFrom":subQ3}),-1.0]])]});}
            var Q44;
            {var subQ0=sQuery(id+"F0.wireOp",EDGE,"kBsuryHM-TEui-fzTh-jwx4-rL4DmjWNnCFb");Q44=makeQuery(id+"F0.imprint","IMPRINT",FACE,{"disambiguationData":[TD([[makeQuery(id+"F0.imprint","IMPRINT",EDGE,{"derivedFrom":subQ0}),-1.0]])]});}
            var Q45;
            {var subQ1=sQuery(id+"F0.wireOp",EDGE,"P492LHx6-NSug-mfq4-rksP-dPNl1cmWB1kc");var subQ3=sQuery(id+"F0.wireOp",EDGE,"2FP64cKd-Qtdr-E4Ue-gX8b-GauW4VJF4Wkc");var subQ4=makeQuery(id+"F0.imprint","INTERSECT",VERTEX,{"derivedFrom":[subQ1,subQ3]});Q45=makeQuery(id+"F0.imprint","IMPRINT",FACE,{"disambiguationData":[TD([[makeQuery(id+"F0.imprint","IMPRINT",EDGE,{"disambiguationData":[TD([[subQ4,-1.0]])],"derivedFrom":subQ3}),-1.0]])]});}
            var Q46;
            {var subQ0=sQuery(id+"F0.wireOp",EDGE,"YMZMJfLn-nZsa-23N9-HD2U-rS3wBJQ1yxtU");Q46=makeQuery(id+"F0.imprint","IMPRINT",FACE,{"disambiguationData":[TD([[makeQuery(id+"F0.imprint","IMPRINT",EDGE,{"derivedFrom":subQ0}),1.0]])]});}
            var Q47;
            {var subQ0=sQuery(id+"F0.wireOp",EDGE,"2FP64cKd-Qtdr-E4Ue-gX8b-GauW4VJF4Wkc");var subQ1=sQuery(id+"F0.wireOp",EDGE,"P492LHx6-NSug-mfq4-rksP-dPNl1cmWB1kc");var subQ2=makeQuery(id+"F0.imprint","INTERSECT",VERTEX,{"derivedFrom":[subQ1,subQ0]});Q47=makeQuery(id+"F0.imprint","IMPRINT",FACE,{"disambiguationData":[TD([[makeQuery(id+"F0.imprint","IMPRINT",EDGE,{"disambiguationData":[TD([[subQ2,-1.0]])],"derivedFrom":subQ1}),1.0]])]});}
            var Q48;
            {var subQ0=sQuery(id+"F0.wireOp",EDGE,"E274");Q48=makeQuery(id+"F0.imprint","IMPRINT",FACE,{"disambiguationData":[TD([[makeQuery(id+"F0.imprint","IMPRINT",EDGE,{"derivedFrom":subQ0}),1.0]])]});}
            var Q49;
            {var subQ0=sQuery(id+"F0.wireOp",EDGE,"E282");Q49=makeQuery(id+"F0.imprint","IMPRINT",FACE,{"disambiguationData":[TD([[makeQuery(id+"F0.imprint","IMPRINT",EDGE,{"derivedFrom":subQ0}),-1.0]])]});}
            var Q50;
            {var subQ1=sQuery(id+"F0.wireOp",EDGE,"E286.bottom");Q50=makeQuery(id+"F0.imprint","IMPRINT",FACE,{"disambiguationData":[TD([[makeQuery(id+"F0.imprint","IMPRINT",EDGE,{"derivedFrom":subQ1}),-1.0]])]});}
            var Q51;
            {var subQ6=sQuery(id+"F0.wireOp",EDGE,"E286.left");Q51=makeQuery(id+"F0.imprint","IMPRINT",FACE,{"disambiguationData":[TD([[makeQuery(id+"F0.imprint","IMPRINT",EDGE,{"derivedFrom":subQ6}),-1.0]])]});}
            var Q52;
            {var subQ0=sQuery(id+"F0.wireOp",EDGE,"E319");Q52=makeQuery(id+"F0.imprint","IMPRINT",FACE,{"disambiguationData":[TD([[makeQuery(id+"F0.imprint","IMPRINT",EDGE,{"derivedFrom":subQ0}),-1.0]])]});}
            var Q53;
            {var subQ0=sQuery(id+"F0.wireOp",EDGE,"E302");Q53=makeQuery(id+"F0.imprint","IMPRINT",FACE,{"disambiguationData":[TD([[makeQuery(id+"F0.imprint","IMPRINT",EDGE,{"derivedFrom":subQ0}),-1.0]])]});}
            var Q54;
            {var subQ4=sQuery(id+"F0.wireOp",EDGE,"E302");Q54=makeQuery(id+"F0.imprint","IMPRINT",FACE,{"disambiguationData":[TD([[makeQuery(id+"F0.imprint","IMPRINT",EDGE,{"derivedFrom":subQ4}),1.0]])]});}
            var Q55;
            {var subQ2=sQuery(id+"F0.wireOp",EDGE,"E295");Q55=makeQuery(id+"F0.imprint","IMPRINT",FACE,{"disambiguationData":[TD([[makeQuery(id+"F0.imprint","IMPRINT",EDGE,{"derivedFrom":subQ2}),-1.0]])]});}
            var Q56;
            Q56=makeQuery(id+"F0.imprint","IMPRINT",FACE,{"disambiguationData":[TD([[makeQuery(id+"F0.imprint","IMPRINT",EDGE,{"derivedFrom":sQuery(id+"F0.wireOp",EDGE,"E290")}),-1.0]])]});
            var Q57;
            {var subQ0=sQuery(id+"F0.wireOp",EDGE,"E293");Q57=makeQuery(id+"F0.imprint","IMPRINT",FACE,{"disambiguationData":[TD([[makeQuery(id+"F0.imprint","IMPRINT",EDGE,{"derivedFrom":subQ0}),-1.0]])]});}
            extrude(context, id + "F2", {"entities" : qUnion([Q0, Q1, Q2, Q3, Q4, Q5, Q6, Q7, Q8, Q9, Q10, Q11, Q12, Q13, Q14, Q15, Q16, Q17, Q18, Q19, Q20, Q21, Q22, Q23, Q24, Q25, Q26, Q27, Q28, Q29, Q30, Q31, Q32, Q33, Q34, Q35, Q36, Q37, Q38, Q39, Q40, Q41, Q42, Q43, Q44, Q45, Q46, Q47, Q48, Q49, Q50, Q51, Q52, Q53, Q54, Q55, Q56, Q57]), "depth" : 5.08 * mm, "offsetDistance" : 25 * mm});
        }
        {
            var Q0;
            Q0=makeQuery(id+"F2.opExtrude","SWEPT_EDGE",EDGE,{"disambiguationData":[OSD([sQuery(id+"F0.wireOp",EDGE,"phCxUf2S-gZjV-f4xv-aas1-PVqHYAnoji5H"),sQuery(id+"F0.wireOp",EDGE,"xtBT87Da-3AQh-zfyC-tqdO-VPEidZ8M0z3L")])]});
            var Q1;
            Q1=makeQuery(id+"F2.opExtrude","SWEPT_EDGE",EDGE,{"disambiguationData":[OSD([sQuery(id+"F0.wireOp",EDGE,"E170.bottom"),sQuery(id+"F0.wireOp",EDGE,"E170.right"),sQuery(id+"F0.wireOp",EDGE,"nD8obWDZ-dazQ-llHs-Izlf-LJ3wYFsX20le")])]});
            var Q2;
            Q2=makeQuery(id+"F2.opExtrude","SWEPT_EDGE",EDGE,{"disambiguationData":[OSD([sQuery(id+"F0.wireOp",EDGE,"LLzZ3JUF-ulNa-C1tB-ibGi-thdqKUuZeLZg"),sQuery(id+"F0.wireOp",EDGE,"h3wgar6C-z9Do-TTWB-thoL-HvqMpJdKu6Du")])]});
            var Q3;
            Q3=makeQuery(id+"F2.opExtrude","SWEPT_EDGE",EDGE,{"disambiguationData":[OSD([sQuery(id+"F0.wireOp",EDGE,"E170.bottom"),sQuery(id+"F0.wireOp",EDGE,"E170.left"),sQuery(id+"F0.wireOp",EDGE,"nsFH2kIf-Hh6N-lDFP-sCm9-CDu6dfWFGG9B")])]});
            var Q4;
            Q4=makeQuery(id+"F2.opExtrude","SWEPT_EDGE",EDGE,{"disambiguationData":[OSD([sQuery(id+"F0.wireOp",EDGE,"E184"),sQuery(id+"F0.wireOp",EDGE,"E185")])]});
            var Q5;
            Q5=makeQuery(id+"F2.opExtrude","SWEPT_EDGE",EDGE,{"disambiguationData":[OSD([sQuery(id+"F0.wireOp",EDGE,"E181"),sQuery(id+"F0.wireOp",EDGE,"E182")])]});
            var Q6;
            Q6=makeQuery(id+"F2.opExtrude","SWEPT_EDGE",EDGE,{"disambiguationData":[OSD([sQuery(id+"F0.wireOp",EDGE,"E226"),sQuery(id+"F0.wireOp",EDGE,"E227")])]});
            var Q7;
            Q7=makeQuery(id+"F2.opExtrude","SWEPT_EDGE",EDGE,{"disambiguationData":[OSD([sQuery(id+"F0.wireOp",EDGE,"E228"),sQuery(id+"F0.wireOp",EDGE,"E229")])]});
            var Q8;
            Q8=makeQuery(id+"F2.opExtrude","SWEPT_EDGE",EDGE,{"disambiguationData":[OSD([sQuery(id+"F0.wireOp",EDGE,"E243.MirrorCS"),sQuery(id+"F0.wireOp",EDGE,"E244.MirrorCS")])]});
            var Q9;
            Q9=makeQuery(id+"F2.opExtrude","SWEPT_EDGE",EDGE,{"disambiguationData":[OSD([sQuery(id+"F0.wireOp",EDGE,"E239"),sQuery(id+"F0.wireOp",EDGE,"E240")])]});
            var Q10;
            Q10=makeQuery(id+"F2.opExtrude","SWEPT_EDGE",EDGE,{"disambiguationData":[OSD([sQuery(id+"F0.wireOp",EDGE,"E274"),sQuery(id+"F0.wireOp",EDGE,"E276")])]});
            var Q11;
            Q11=makeQuery(id+"F2.opExtrude","SWEPT_EDGE",EDGE,{"disambiguationData":[OSD([sQuery(id+"F0.wireOp",EDGE,"E311"),sQuery(id+"F0.wireOp",EDGE,"E313")])]});
            var Q12;
            Q12=makeQuery(id+"F2.opExtrude","SWEPT_EDGE",EDGE,{"disambiguationData":[OSD([sQuery(id+"F0.wireOp",EDGE,"E286.bottom"),sQuery(id+"F0.wireOp",EDGE,"E286.left"),sQuery(id+"F0.wireOp",EDGE,"E311")])]});
            var Q13;
            Q13=makeQuery(id+"F2.opExtrude","SWEPT_EDGE",EDGE,{"disambiguationData":[OSD([sQuery(id+"F0.wireOp",EDGE,"E286.bottom"),sQuery(id+"F0.wireOp",EDGE,"E286.right"),sQuery(id+"F0.wireOp",EDGE,"E297")])]});
            var Q14;
            Q14=makeQuery(id+"F2.opExtrude","SWEPT_EDGE",EDGE,{"disambiguationData":[OSD([sQuery(id+"F0.wireOp",EDGE,"E297"),sQuery(id+"F0.wireOp",EDGE,"E298")])]});
            var Q15;
            Q15=makeQuery(id+"F2.opExtrude","SWEPT_EDGE",EDGE,{"disambiguationData":[OSD([sQuery(id+"F0.wireOp",EDGE,"E293"),sQuery(id+"F0.wireOp",EDGE,"E294"),sQuery(id+"F0.wireOp",EDGE,"E301"),sQuery(id+"F0.wireOp",EDGE,"E313")])]});
            var Q16;
            Q16=makeQuery(id+"F1.opExtrude","SWEPT_EDGE",EDGE,{"disambiguationData":[OSD([sQuery(id+"F0.wireOp",EDGE,"E100.bottom"),sQuery(id+"F0.wireOp",EDGE,"E100.right"),sQuery(id+"F0.wireOp",EDGE,"bccfaa52-02d4-4c2e-89ca-5f6b09c8004b.MirrorCS")])]});
            var Q17;
            Q17=makeQuery(id+"F1.opExtrude","SWEPT_EDGE",EDGE,{"disambiguationData":[OSD([sQuery(id+"F0.wireOp",EDGE,"E100.bottom"),sQuery(id+"F0.wireOp",EDGE,"E100.left"),sQuery(id+"F0.wireOp",EDGE,"E106")])]});
            fillet(context, id + "F3", {"entities" : qUnion([Q0, Q1, Q2, Q3, Q4, Q5, Q6, Q7, Q8, Q9, Q10, Q11, Q12, Q13, Q14, Q15, Q16, Q17]), "radius" : 5 * mm, "tangentPropagation" : true, "allowEdgeOverflow" : false});
        }
        {
            var Q0;
            Q0=makeQuery(id+"F2.opExtrude","SWEPT_EDGE",EDGE,{"disambiguationData":[OSD([sQuery(id+"F0.wireOp",EDGE,"E210"),sQuery(id+"F0.wireOp",EDGE,"E213")])]});
            var Q1;
            Q1=makeQuery(id+"F2.opExtrude","SWEPT_EDGE",EDGE,{"disambiguationData":[OSD([sQuery(id+"F0.wireOp",EDGE,"E212"),sQuery(id+"F0.wireOp",EDGE,"E213")])]});
            var Q2;
            Q2=makeQuery(id+"F2.opExtrude","SWEPT_EDGE",EDGE,{"disambiguationData":[OSD([sQuery(id+"F0.wireOp",EDGE,"E211"),sQuery(id+"F0.wireOp",EDGE,"E212")])]});
            var Q3;
            Q3=makeQuery(id+"F2.opExtrude","SWEPT_EDGE",EDGE,{"disambiguationData":[OSD([sQuery(id+"F0.wireOp",EDGE,"E215"),sQuery(id+"F0.wireOp",EDGE,"E216")])]});
            var Q4;
            Q4=makeQuery(id+"F2.opExtrude","SWEPT_EDGE",EDGE,{"disambiguationData":[OSD([sQuery(id+"F0.wireOp",EDGE,"E214"),sQuery(id+"F0.wireOp",EDGE,"E217")])]});
            var Q5;
            Q5=makeQuery(id+"F2.opExtrude","SWEPT_EDGE",EDGE,{"disambiguationData":[OSD([sQuery(id+"F0.wireOp",EDGE,"E223"),sQuery(id+"F0.wireOp",EDGE,"E224")])]});
            var Q6;
            Q6=makeQuery(id+"F2.opExtrude","SWEPT_EDGE",EDGE,{"disambiguationData":[OSD([sQuery(id+"F0.wireOp",EDGE,"E222"),sQuery(id+"F0.wireOp",EDGE,"E223")])]});
            var Q7;
            Q7=makeQuery(id+"F2.opExtrude","SWEPT_EDGE",EDGE,{"disambiguationData":[OSD([sQuery(id+"F0.wireOp",EDGE,"E219"),sQuery(id+"F0.wireOp",EDGE,"E220")])]});
            var Q8;
            Q8=makeQuery(id+"F2.opExtrude","SWEPT_EDGE",EDGE,{"disambiguationData":[OSD([sQuery(id+"F0.wireOp",EDGE,"E220"),sQuery(id+"F0.wireOp",EDGE,"E224")])]});
            var Q9;
            Q9=makeQuery(id+"F2.opExtrude","SWEPT_EDGE",EDGE,{"disambiguationData":[OSD([sQuery(id+"F0.wireOp",EDGE,"E235"),sQuery(id+"F0.wireOp",EDGE,"E236")])]});
            var Q10;
            Q10=makeQuery(id+"F2.opExtrude","SWEPT_EDGE",EDGE,{"disambiguationData":[OSD([sQuery(id+"F0.wireOp",EDGE,"E232"),sQuery(id+"F0.wireOp",EDGE,"E236")])]});
            fillet(context, id + "F4", {"entities" : qUnion([Q0, Q1, Q2, Q3, Q4, Q5, Q6, Q7, Q8, Q9, Q10]), "radius" : 3.5 * mm, "tangentPropagation" : true, "allowEdgeOverflow" : false});
        }
        {
            var Q0;
            Q0=makeQuery(id+"F2.opExtrude","SWEPT_EDGE",EDGE,{"disambiguationData":[OSD([sQuery(id+"F0.wireOp",EDGE,"E221"),sQuery(id+"F0.wireOp",EDGE,"E222")])]});
            var Q1;
            Q1=makeQuery(id+"F2.opExtrude","SWEPT_EDGE",EDGE,{"disambiguationData":[OSD([sQuery(id+"F0.wireOp",EDGE,"E219"),sQuery(id+"F0.wireOp",EDGE,"E221")])]});
            var Q2;
            Q2=makeQuery(id+"F2.opExtrude","SWEPT_EDGE",EDGE,{"disambiguationData":[OSD([sQuery(id+"F0.wireOp",EDGE,"E233"),sQuery(id+"F0.wireOp",EDGE,"E234")])]});
            var Q3;
            Q3=makeQuery(id+"F2.opExtrude","SWEPT_EDGE",EDGE,{"disambiguationData":[OSD([sQuery(id+"F0.wireOp",EDGE,"E231"),sQuery(id+"F0.wireOp",EDGE,"E233")])]});
            var Q4;
            Q4=makeQuery(id+"F1.opExtrude","SWEPT_EDGE",EDGE,{"disambiguationData":[OSD([sQuery(id+"F0.wireOp",EDGE,"E334.bottom"),sQuery(id+"F0.wireOp",EDGE,"E335.bottom"),sQuery(id+"F0.wireOp",EDGE,"E335.right")])]});
            var Q5;
            Q5=makeQuery(id+"F1.opExtrude","SWEPT_EDGE",EDGE,{"disambiguationData":[OSD([sQuery(id+"F0.wireOp",EDGE,"E334.bottom"),sQuery(id+"F0.wireOp",EDGE,"E335.bottom"),sQuery(id+"F0.wireOp",EDGE,"E335.left")])]});
            var Q6;
            Q6=makeQuery(id+"F1.opExtrude","SWEPT_EDGE",EDGE,{"disambiguationData":[OSD([sQuery(id+"F0.wireOp",EDGE,"E334.top"),sQuery(id+"F0.wireOp",EDGE,"E335.top"),sQuery(id+"F0.wireOp",EDGE,"E335.left")])]});
            var Q7;
            Q7=makeQuery(id+"F1.opExtrude","SWEPT_EDGE",EDGE,{"disambiguationData":[OSD([sQuery(id+"F0.wireOp",EDGE,"E334.top"),sQuery(id+"F0.wireOp",EDGE,"E335.top"),sQuery(id+"F0.wireOp",EDGE,"E335.right")])]});
            var Q8;
            Q8=makeQuery(id+"F1.opExtrude","SWEPT_EDGE",EDGE,{"disambiguationData":[OSD([sQuery(id+"F0.wireOp",EDGE,"E334.top"),sQuery(id+"F0.wireOp",EDGE,"E336.top"),sQuery(id+"F0.wireOp",EDGE,"E336.right")])]});
            var Q9;
            Q9=makeQuery(id+"F1.opExtrude","SWEPT_EDGE",EDGE,{"disambiguationData":[OSD([sQuery(id+"F0.wireOp",EDGE,"E334.top"),sQuery(id+"F0.wireOp",EDGE,"E337.top"),sQuery(id+"F0.wireOp",EDGE,"E337.right")])]});
            var Q10;
            Q10=makeQuery(id+"F1.opExtrude","SWEPT_EDGE",EDGE,{"disambiguationData":[OSD([sQuery(id+"F0.wireOp",EDGE,"E334.top"),sQuery(id+"F0.wireOp",EDGE,"E338.top"),sQuery(id+"F0.wireOp",EDGE,"E338.right")])]});
            var Q11;
            Q11=makeQuery(id+"F1.opExtrude","SWEPT_EDGE",EDGE,{"disambiguationData":[OSD([sQuery(id+"F0.wireOp",EDGE,"E334.top"),sQuery(id+"F0.wireOp",EDGE,"E336.top"),sQuery(id+"F0.wireOp",EDGE,"E336.left")])]});
            var Q12;
            Q12=makeQuery(id+"F1.opExtrude","SWEPT_EDGE",EDGE,{"disambiguationData":[OSD([sQuery(id+"F0.wireOp",EDGE,"E334.top"),sQuery(id+"F0.wireOp",EDGE,"E337.top"),sQuery(id+"F0.wireOp",EDGE,"E337.left")])]});
            var Q13;
            Q13=makeQuery(id+"F1.opExtrude","SWEPT_EDGE",EDGE,{"disambiguationData":[OSD([sQuery(id+"F0.wireOp",EDGE,"E334.top"),sQuery(id+"F0.wireOp",EDGE,"E338.top"),sQuery(id+"F0.wireOp",EDGE,"E338.left")])]});
            var Q14;
            Q14=makeQuery(id+"F1.opExtrude","SWEPT_EDGE",EDGE,{"disambiguationData":[OSD([sQuery(id+"F0.wireOp",EDGE,"E334.bottom"),sQuery(id+"F0.wireOp",EDGE,"E336.bottom"),sQuery(id+"F0.wireOp",EDGE,"E336.left")])]});
            var Q15;
            Q15=makeQuery(id+"F1.opExtrude","SWEPT_EDGE",EDGE,{"disambiguationData":[OSD([sQuery(id+"F0.wireOp",EDGE,"E334.bottom"),sQuery(id+"F0.wireOp",EDGE,"E337.bottom"),sQuery(id+"F0.wireOp",EDGE,"E337.left")])]});
            var Q16;
            Q16=makeQuery(id+"F1.opExtrude","SWEPT_EDGE",EDGE,{"disambiguationData":[OSD([sQuery(id+"F0.wireOp",EDGE,"E334.bottom"),sQuery(id+"F0.wireOp",EDGE,"E338.bottom"),sQuery(id+"F0.wireOp",EDGE,"E338.left")])]});
            var Q17;
            Q17=makeQuery(id+"F1.opExtrude","SWEPT_EDGE",EDGE,{"disambiguationData":[OSD([sQuery(id+"F0.wireOp",EDGE,"E334.bottom"),sQuery(id+"F0.wireOp",EDGE,"E338.bottom"),sQuery(id+"F0.wireOp",EDGE,"E338.right")])]});
            var Q18;
            Q18=makeQuery(id+"F1.opExtrude","SWEPT_EDGE",EDGE,{"disambiguationData":[OSD([sQuery(id+"F0.wireOp",EDGE,"E334.bottom"),sQuery(id+"F0.wireOp",EDGE,"E336.bottom"),sQuery(id+"F0.wireOp",EDGE,"E336.right")])]});
            var Q19;
            Q19=makeQuery(id+"F1.opExtrude","SWEPT_EDGE",EDGE,{"disambiguationData":[OSD([sQuery(id+"F0.wireOp",EDGE,"E334.bottom"),sQuery(id+"F0.wireOp",EDGE,"E337.bottom"),sQuery(id+"F0.wireOp",EDGE,"E337.right")])]});
            var Q20;
            Q20=makeQuery(id+"F1.opExtrude","SWEPT_EDGE",EDGE,{"disambiguationData":[OSD([sQuery(id+"F0.wireOp",EDGE,"E339.bottom"),sQuery(id+"F0.wireOp",EDGE,"E339.right")])]});
            var Q21;
            Q21=makeQuery(id+"F1.opExtrude","SWEPT_EDGE",EDGE,{"disambiguationData":[OSD([sQuery(id+"F0.wireOp",EDGE,"E340.MirrorCS"),sQuery(id+"F0.wireOp",EDGE,"E341.MirrorCS")])]});
            var Q22;
            Q22=makeQuery(id+"F1.opExtrude","SWEPT_EDGE",EDGE,{"disambiguationData":[OSD([sQuery(id+"F0.wireOp",EDGE,"E341.MirrorCS"),sQuery(id+"F0.wireOp",EDGE,"E342.MirrorCS")])]});
            var Q23;
            Q23=makeQuery(id+"F1.opExtrude","SWEPT_EDGE",EDGE,{"disambiguationData":[OSD([sQuery(id+"F0.wireOp",EDGE,"E339.bottom"),sQuery(id+"F0.wireOp",EDGE,"E339.left")])]});
            var Q24;
            Q24=makeQuery(id+"F1.opExtrude","SWEPT_EDGE",EDGE,{"disambiguationData":[OSD([sQuery(id+"F0.wireOp",EDGE,"E342.MirrorCS"),sQuery(id+"F0.wireOp",EDGE,"E343.MirrorCS")])]});
            var Q25;
            Q25=makeQuery(id+"F1.opExtrude","SWEPT_EDGE",EDGE,{"disambiguationData":[OSD([sQuery(id+"F0.wireOp",EDGE,"E340.MirrorCS"),sQuery(id+"F0.wireOp",EDGE,"E343.MirrorCS")])]});
            var Q26;
            Q26=makeQuery(id+"F1.opExtrude","SWEPT_EDGE",EDGE,{"disambiguationData":[OSD([sQuery(id+"F0.wireOp",EDGE,"E339.top"),sQuery(id+"F0.wireOp",EDGE,"E339.right")])]});
            var Q27;
            Q27=makeQuery(id+"F1.opExtrude","SWEPT_EDGE",EDGE,{"disambiguationData":[OSD([sQuery(id+"F0.wireOp",EDGE,"E339.top"),sQuery(id+"F0.wireOp",EDGE,"E339.left")])]});
            fillet(context, id + "F5", {"entities" : qUnion([Q0, Q1, Q2, Q3, Q4, Q5, Q6, Q7, Q8, Q9, Q10, Q11, Q12, Q13, Q14, Q15, Q16, Q17, Q18, Q19, Q20, Q21, Q22, Q23, Q24, Q25, Q26, Q27]), "radius" : 1 * mm, "tangentPropagation" : true, "allowEdgeOverflow" : false});
        }
    });
